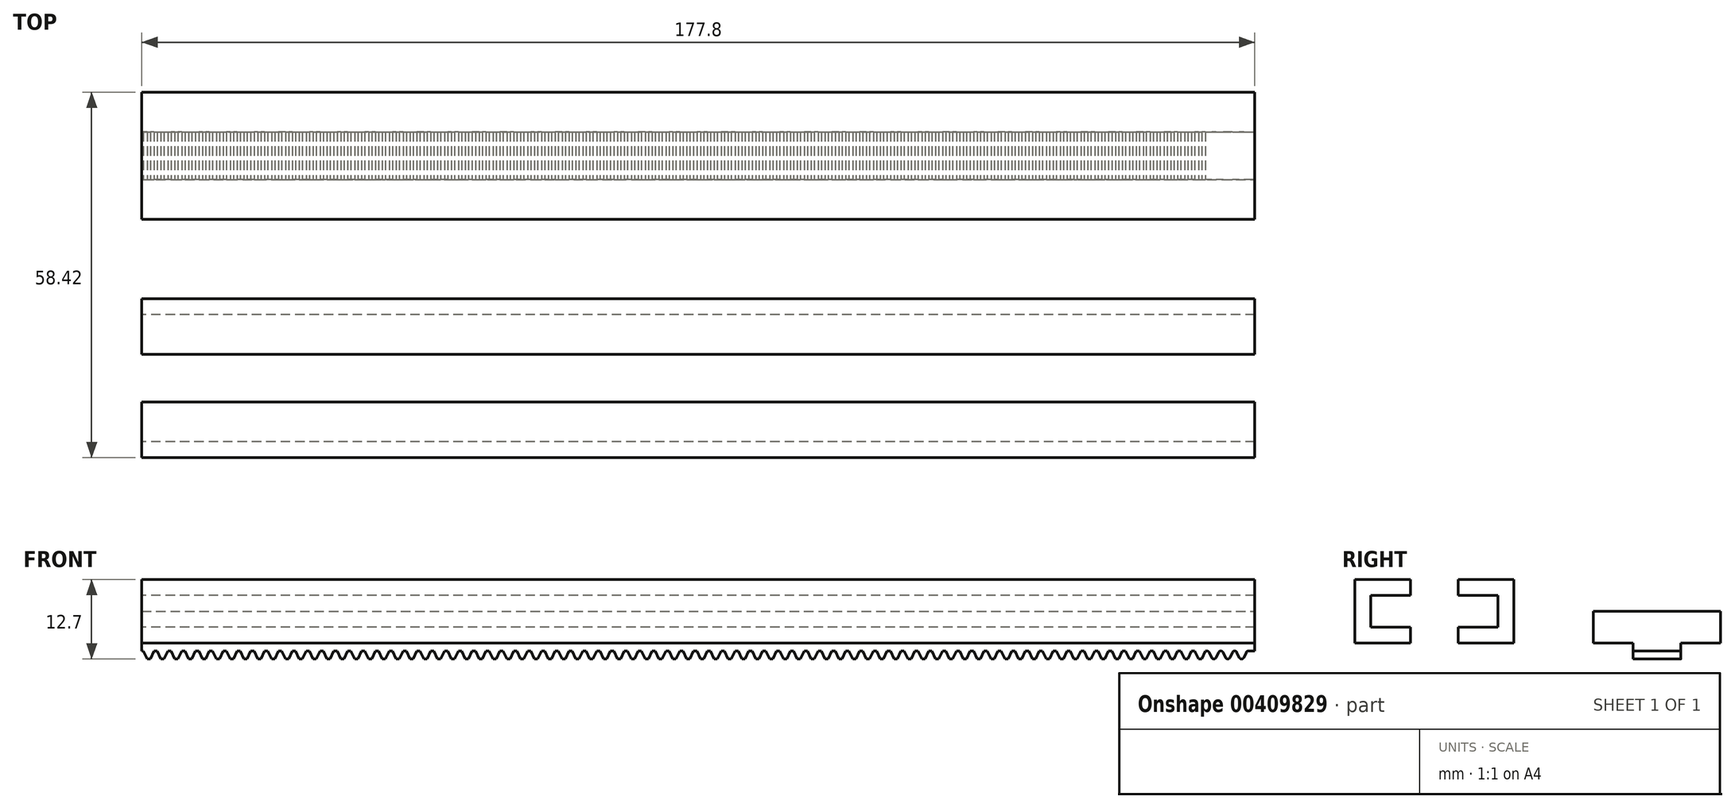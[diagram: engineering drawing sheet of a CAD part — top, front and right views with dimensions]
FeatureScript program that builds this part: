
annotation { "Feature Type Name" : "Feature", "Feature Type Description" : "" }
export const myFeature = defineFeature(function(context is Context, id is Id, definition is map)
    precondition{}
    {
        {
            var Q0;
            Q0=qCreatedBy(makeId("Front.planeOp"),FACE);
            var sketch = newSketch(context, id + "F0", { "sketchPlane" : qUnion([Q0])});
            skLineSegment(sketch, "E0.bottom", {"start": v(0, 0) * mm, "end": v(-177.8, 0) * mm});
            skLineSegment(sketch, "E0.top", {"start": v(0, 10.16) * mm, "end": v(-177.8, 10.16) * mm});
            skLineSegment(sketch, "E0.left", {"start": v(0, 0) * mm, "end": v(0, 10.16) * mm});
            skLineSegment(sketch, "E0.right", {"start": v(-177.8, 0) * mm, "end": v(-177.8, 10.16) * mm});
            skSolve(sketch);
        }
        {
            var Q0;
            Q0=makeQuery(id+"F0.imprint","IMPRINT",FACE,{"disambiguationData":[TD([[makeQuery(id+"F0.imprint","IMPRINT",EDGE,{"derivedFrom":sQuery(id+"F0.wireOp",EDGE,"E0.bottom")}),-1.0]])]});
            extrude(context, id + "F1", {"entities" : qUnion([Q0]), "depth" : 25.4 * mm});
        }
        {
            var Q0;
            Q0=makeQuery(id+"F1.opExtrude","SWEPT_FACE",FACE,{"disambiguationData":[OSD([sQuery(id+"F0.wireOp",EDGE,"E0.right")])]});
            shell(context, id + "F2", {"entities" : qUnion([Q0]), "thickness" : 2.54 * mm});
        }
        {
            var Q0;
            Q0=makeQuery(id+"F2.opShell","OFFSET_FACE",FACE,{"disambiguationData":[OSD([sQuery(id+"F0.wireOp",EDGE,"E0.left")])]});
            extrude(context, id + "F3", {"entities" : qUnion([Q0]), "operationType" : NewBodyOperationType.REMOVE, "oppositeDirection" : true, "depth" : 25.4 * mm});
        }
        {
            var Q0;
            Q0=makeQuery(id+"F1.opExtrude","SWEPT_FACE",FACE,{"disambiguationData":[OSD([sQuery(id+"F0.wireOp",EDGE,"E0.top")])]});
            var sketch = newSketch(context, id + "F4", { "sketchPlane" : qUnion([Q0])});
            skLineSegment(sketch, "E1.bottom", {"start": v(-177.8, -8.9) * mm, "end": v(0, -8.89) * mm});
            skLineSegment(sketch, "E1.top", {"start": v(-177.8, -16.51) * mm, "end": v(0, -16.5) * mm});
            skLineSegment(sketch, "E1.left", {"start": v(-177.8, -8.9) * mm, "end": v(-177.8, -16.51) * mm});
            skLineSegment(sketch, "E1.right", {"start": v(0, -8.89) * mm, "end": v(0, -16.5) * mm});
            skSolve(sketch);
        }
        {
            var Q0;
            Q0=makeQuery(id+"F4.imprint","IMPRINT",FACE,{"disambiguationData":[TD([[makeQuery(id+"F4.imprint","IMPRINT",EDGE,{"derivedFrom":sQuery(id+"F4.wireOp",EDGE,"E1.bottom")}),-1.0]])]});
            extrude(context, id + "F5", {"entities" : qUnion([Q0]), "operationType" : NewBodyOperationType.REMOVE, "oppositeDirection" : true, "depth" : 25.4 * mm});
        }
        {
            var Q0;
            Q0=qCreatedBy(makeId("Right.planeOp"),FACE);
            var sketch = newSketch(context, id + "F6", { "sketchPlane" : qUnion([Q0])});
            skLineSegment(sketch, "E2.bottom", {"start": v(12.7, 0) * mm, "end": v(33.02, 0) * mm});
            skLineSegment(sketch, "E2.top", {"start": v(12.7, 5.08) * mm, "end": v(33.02, 5.08) * mm});
            skLineSegment(sketch, "E2.left", {"start": v(12.7, 0) * mm, "end": v(12.7, 5.08) * mm});
            skLineSegment(sketch, "E2.right", {"start": v(33.02, 0) * mm, "end": v(33.02, 5.08) * mm});
            skLineSegment(sketch, "E3", {"start": v(12.7, 0) * mm, "end": v(19.05, 0) * mm});
            skLineSegment(sketch, "E4", {"start": v(19.05, 0) * mm, "end": v(19.05, -2.54) * mm});
            skLineSegment(sketch, "E5", {"start": v(19.05, -2.54) * mm, "end": v(26.67, -2.54) * mm});
            skLineSegment(sketch, "E6", {"start": v(26.67, -2.54) * mm, "end": v(26.67, 0) * mm});
            skLineSegment(sketch, "E7", {"start": v(26.67, 0) * mm, "end": v(33.02, 0) * mm});
            skSolve(sketch);
        }
        {
            var Q0;
            Q0=makeQuery(id+"F6.imprint","IMPRINT",FACE,{"disambiguationData":[TD([[makeQuery(id+"F6.imprint","IMPRINT",EDGE,{"derivedFrom":sQuery(id+"F6.wireOp",EDGE,"E2.bottom")}),-1.0]])]});
            var Q1;
            Q1=makeQuery(id+"F6.imprint","IMPRINT",FACE,{"disambiguationData":[TD([[makeQuery(id+"F6.imprint","IMPRINT",EDGE,{"derivedFrom":sQuery(id+"F6.wireOp",EDGE,"E2.bottom")}),1.0]])]});
            extrude(context, id + "F7", {"entities" : qUnion([Q0, Q1]), "oppositeDirection" : true, "depth" : 177.8 * mm});
        }
        {
            var Q0;
            Q0=makeQuery(id+"F7.opExtrude","SWEPT_FACE",FACE,{"disambiguationData":[OSD([sQuery(id+"F6.wireOp",EDGE,"E4")])]});
            var sketch = newSketch(context, id + "F8", { "sketchPlane" : qUnion([Q0])});
            skLineSegment(sketch, "E8", {"start": v(-177.8, -1.27) * mm, "end": v(-177.54, -1.27) * mm});
            skLineSegment(sketch, "E9", {"start": v(-177.54, -1.27) * mm, "end": v(-176.94, -2.54) * mm});
            skLineSegment(sketch, "E10", {"start": v(-176.94, -2.54) * mm, "end": v(-176.44, -2.54) * mm});
            skLineSegment(sketch, "E11", {"start": v(-176.44, -2.54) * mm, "end": v(-175.84, -1.27) * mm});
            skLineSegment(sketch, "E12", {"start": v(-175.84, -1.27) * mm, "end": v(-175.6, -1.27) * mm});
            skLineSegment(sketch, "E13.MirrorCS", {"start": v(-175.34, -1.27) * mm, "end": v(-175.6, -1.27) * mm});
            skLineSegment(sketch, "E14.MirrorCS", {"start": v(-174.74, -2.54) * mm, "end": v(-175.34, -1.27) * mm});
            skLineSegment(sketch, "E15.MirrorCS", {"start": v(-174.24, -2.54) * mm, "end": v(-174.74, -2.54) * mm});
            skLineSegment(sketch, "E16.MirrorCS", {"start": v(-173.64, -1.27) * mm, "end": v(-174.24, -2.54) * mm});
            skLineSegment(sketch, "E17.MirrorCS", {"start": v(-173.38, -1.27) * mm, "end": v(-173.64, -1.27) * mm});
            skLineSegment(sketch, "E18.MirrorCS", {"start": v(-173.38, -1.27) * mm, "end": v(-173.12, -1.27) * mm});
            skLineSegment(sketch, "E19.MirrorCS", {"start": v(-173.12, -1.27) * mm, "end": v(-172.52, -2.54) * mm});
            skLineSegment(sketch, "E20.MirrorCS", {"start": v(-172.52, -2.54) * mm, "end": v(-172.02, -2.54) * mm});
            skLineSegment(sketch, "E21.MirrorCS", {"start": v(-172.02, -2.54) * mm, "end": v(-171.42, -1.27) * mm});
            skLineSegment(sketch, "E22.MirrorCS", {"start": v(-171.42, -1.27) * mm, "end": v(-171.17, -1.27) * mm});
            skLineSegment(sketch, "E23.MirrorCS", {"start": v(-170.92, -1.27) * mm, "end": v(-171.17, -1.27) * mm});
            skLineSegment(sketch, "E24.MirrorCS", {"start": v(-170.32, -2.54) * mm, "end": v(-170.92, -1.27) * mm});
            skLineSegment(sketch, "E25.MirrorCS", {"start": v(-169.82, -2.54) * mm, "end": v(-170.32, -2.54) * mm});
            skLineSegment(sketch, "E26.MirrorCS", {"start": v(-169.22, -1.27) * mm, "end": v(-169.82, -2.54) * mm});
            skLineSegment(sketch, "E27.MirrorCS", {"start": v(-168.96, -1.27) * mm, "end": v(-169.22, -1.27) * mm});
            skLineSegment(sketch, "E28.MirrorCS", {"start": v(-164.54, -1.27) * mm, "end": v(-164.28, -1.27) * mm});
            skLineSegment(sketch, "E29.MirrorCS", {"start": v(-164.54, -1.27) * mm, "end": v(-164.8, -1.27) * mm});
            skLineSegment(sketch, "E30.MirrorCS", {"start": v(-162.58, -1.27) * mm, "end": v(-162.33, -1.27) * mm});
            skLineSegment(sketch, "E31.MirrorCS", {"start": v(-162.08, -1.27) * mm, "end": v(-162.33, -1.27) * mm});
            skLineSegment(sketch, "E32.MirrorCS", {"start": v(-160.12, -1.27) * mm, "end": v(-160.38, -1.27) * mm});
            skLineSegment(sketch, "E33.MirrorCS", {"start": v(-161.48, -2.54) * mm, "end": v(-162.08, -1.27) * mm});
            skLineSegment(sketch, "E34.MirrorCS", {"start": v(-160.98, -2.54) * mm, "end": v(-161.48, -2.54) * mm});
            skLineSegment(sketch, "E35.MirrorCS", {"start": v(-160.38, -1.27) * mm, "end": v(-160.98, -2.54) * mm});
            skLineSegment(sketch, "E36.MirrorCS", {"start": v(-166.5, -1.27) * mm, "end": v(-166.75, -1.27) * mm});
            skLineSegment(sketch, "E37.MirrorCS", {"start": v(-168.96, -1.27) * mm, "end": v(-168.7, -1.27) * mm});
            skLineSegment(sketch, "E38.MirrorCS", {"start": v(-167, -1.27) * mm, "end": v(-166.75, -1.27) * mm});
            skLineSegment(sketch, "E39.MirrorCS", {"start": v(-164.8, -1.27) * mm, "end": v(-165.4, -2.54) * mm});
            skLineSegment(sketch, "E40.MirrorCS", {"start": v(-164.28, -1.27) * mm, "end": v(-163.68, -2.54) * mm});
            skLineSegment(sketch, "E41.MirrorCS", {"start": v(-168.7, -1.27) * mm, "end": v(-168.1, -2.54) * mm});
            skLineSegment(sketch, "E42.MirrorCS", {"start": v(-163.68, -2.54) * mm, "end": v(-163.18, -2.54) * mm});
            skLineSegment(sketch, "E43.MirrorCS", {"start": v(-167.6, -2.54) * mm, "end": v(-167, -1.27) * mm});
            skLineSegment(sketch, "E44.MirrorCS", {"start": v(-165.4, -2.54) * mm, "end": v(-165.9, -2.54) * mm});
            skLineSegment(sketch, "E45.MirrorCS", {"start": v(-165.9, -2.54) * mm, "end": v(-166.5, -1.27) * mm});
            skLineSegment(sketch, "E46.MirrorCS", {"start": v(-168.1, -2.54) * mm, "end": v(-167.6, -2.54) * mm});
            skLineSegment(sketch, "E47.MirrorCS", {"start": v(-163.18, -2.54) * mm, "end": v(-162.58, -1.27) * mm});
            skLineSegment(sketch, "E48.MirrorCS", {"start": v(-154.84, -2.54) * mm, "end": v(-154.34, -2.54) * mm});
            skLineSegment(sketch, "E49.MirrorCS", {"start": v(-154.34, -2.54) * mm, "end": v(-153.74, -1.27) * mm});
            skLineSegment(sketch, "E50.MirrorCS", {"start": v(-153.24, -1.27) * mm, "end": v(-153.5, -1.27) * mm});
            skLineSegment(sketch, "E51.MirrorCS", {"start": v(-153.74, -1.27) * mm, "end": v(-153.5, -1.27) * mm});
            skLineSegment(sketch, "E52.MirrorCS", {"start": v(-152.14, -2.54) * mm, "end": v(-152.64, -2.54) * mm});
            skLineSegment(sketch, "E53.MirrorCS", {"start": v(-152.64, -2.54) * mm, "end": v(-153.24, -1.27) * mm});
            skLineSegment(sketch, "E54.MirrorCS", {"start": v(-155.7, -1.27) * mm, "end": v(-155.96, -1.27) * mm});
            skLineSegment(sketch, "E55.MirrorCS", {"start": v(-155.7, -1.27) * mm, "end": v(-155.44, -1.27) * mm});
            skLineSegment(sketch, "E56.MirrorCS", {"start": v(-155.44, -1.27) * mm, "end": v(-154.84, -2.54) * mm});
            skLineSegment(sketch, "E57.MirrorCS", {"start": v(-151.28, -1.27) * mm, "end": v(-151.02, -1.27) * mm});
            skLineSegment(sketch, "E58.MirrorCS", {"start": v(-151.28, -1.27) * mm, "end": v(-151.54, -1.27) * mm});
            skLineSegment(sketch, "E59.MirrorCS", {"start": v(-151.54, -1.27) * mm, "end": v(-152.14, -2.54) * mm});
            skLineSegment(sketch, "E60.MirrorCS", {"start": v(-155.96, -1.27) * mm, "end": v(-156.56, -2.54) * mm});
            skLineSegment(sketch, "E61.MirrorCS", {"start": v(-151.02, -1.27) * mm, "end": v(-150.42, -2.54) * mm});
            skLineSegment(sketch, "E62.MirrorCS", {"start": v(-156.56, -2.54) * mm, "end": v(-157.06, -2.54) * mm});
            skLineSegment(sketch, "E63.MirrorCS", {"start": v(-150.42, -2.54) * mm, "end": v(-149.92, -2.54) * mm});
            skLineSegment(sketch, "E64.MirrorCS", {"start": v(-158.16, -1.27) * mm, "end": v(-157.91, -1.27) * mm});
            skLineSegment(sketch, "E65.MirrorCS", {"start": v(-158.76, -2.54) * mm, "end": v(-158.16, -1.27) * mm});
            skLineSegment(sketch, "E66.MirrorCS", {"start": v(-157.66, -1.27) * mm, "end": v(-157.91, -1.27) * mm});
            skLineSegment(sketch, "E67.MirrorCS", {"start": v(-159.26, -2.54) * mm, "end": v(-158.76, -2.54) * mm});
            skLineSegment(sketch, "E68.MirrorCS", {"start": v(-157.06, -2.54) * mm, "end": v(-157.66, -1.27) * mm});
            skLineSegment(sketch, "E69.MirrorCS", {"start": v(-159.86, -1.27) * mm, "end": v(-159.26, -2.54) * mm});
            skLineSegment(sketch, "E70.MirrorCS", {"start": v(-160.12, -1.27) * mm, "end": v(-159.86, -1.27) * mm});
            skLineSegment(sketch, "E71.MirrorCS", {"start": v(-146.86, -1.27) * mm, "end": v(-146.6, -1.27) * mm});
            skLineSegment(sketch, "E72.MirrorCS", {"start": v(-146.86, -1.27) * mm, "end": v(-147.12, -1.27) * mm});
            skLineSegment(sketch, "E73.MirrorCS", {"start": v(-149.92, -2.54) * mm, "end": v(-149.32, -1.27) * mm});
            skLineSegment(sketch, "E74.MirrorCS", {"start": v(-147.72, -2.54) * mm, "end": v(-148.22, -2.54) * mm});
            skLineSegment(sketch, "E75.MirrorCS", {"start": v(-147.12, -1.27) * mm, "end": v(-147.72, -2.54) * mm});
            skLineSegment(sketch, "E76.MirrorCS", {"start": v(-146.6, -1.27) * mm, "end": v(-146, -2.54) * mm});
            skLineSegment(sketch, "E77.MirrorCS", {"start": v(-145.5, -2.54) * mm, "end": v(-144.9, -1.27) * mm});
            skLineSegment(sketch, "E78.MirrorCS", {"start": v(-144.9, -1.27) * mm, "end": v(-144.65, -1.27) * mm});
            skLineSegment(sketch, "E79.MirrorCS", {"start": v(-144.4, -1.27) * mm, "end": v(-144.65, -1.27) * mm});
            skLineSegment(sketch, "E80.MirrorCS", {"start": v(-143.3, -2.54) * mm, "end": v(-143.8, -2.54) * mm});
            skLineSegment(sketch, "E81.MirrorCS", {"start": v(-142.7, -1.27) * mm, "end": v(-143.3, -2.54) * mm});
            skLineSegment(sketch, "E82.MirrorCS", {"start": v(-148.82, -1.27) * mm, "end": v(-149.07, -1.27) * mm});
            skLineSegment(sketch, "E83.MirrorCS", {"start": v(-148.22, -2.54) * mm, "end": v(-148.82, -1.27) * mm});
            skLineSegment(sketch, "E84.MirrorCS", {"start": v(-149.32, -1.27) * mm, "end": v(-149.07, -1.27) * mm});
            skLineSegment(sketch, "E85.MirrorCS", {"start": v(-146, -2.54) * mm, "end": v(-145.5, -2.54) * mm});
            skLineSegment(sketch, "E86.MirrorCS", {"start": v(-142.44, -1.27) * mm, "end": v(-142.7, -1.27) * mm});
            skLineSegment(sketch, "E87.MirrorCS", {"start": v(-143.8, -2.54) * mm, "end": v(-144.4, -1.27) * mm});
            skLineSegment(sketch, "E88.MirrorCS", {"start": v(-129.18, -1.27) * mm, "end": v(-128.92, -1.27) * mm});
            skLineSegment(sketch, "E89.MirrorCS", {"start": v(-129.18, -1.27) * mm, "end": v(-129.44, -1.27) * mm});
            skLineSegment(sketch, "E90.MirrorCS", {"start": v(-131.14, -1.27) * mm, "end": v(-131.4, -1.27) * mm});
            skLineSegment(sketch, "E91.MirrorCS", {"start": v(-131.64, -1.27) * mm, "end": v(-131.4, -1.27) * mm});
            skLineSegment(sketch, "E92.MirrorCS", {"start": v(-117.88, -1.27) * mm, "end": v(-118.13, -1.27) * mm});
            skLineSegment(sketch, "E93.MirrorCS", {"start": v(-118.38, -1.27) * mm, "end": v(-118.13, -1.27) * mm});
            skLineSegment(sketch, "E94.MirrorCS", {"start": v(-120.34, -1.27) * mm, "end": v(-120.08, -1.27) * mm});
            skLineSegment(sketch, "E95.MirrorCS", {"start": v(-120.34, -1.27) * mm, "end": v(-120.6, -1.27) * mm});
            skLineSegment(sketch, "E96.MirrorCS", {"start": v(-119.48, -2.54) * mm, "end": v(-118.98, -2.54) * mm});
            skLineSegment(sketch, "E97.MirrorCS", {"start": v(-130.54, -2.54) * mm, "end": v(-131.14, -1.27) * mm});
            skLineSegment(sketch, "E98.MirrorCS", {"start": v(-118.98, -2.54) * mm, "end": v(-118.38, -1.27) * mm});
            skLineSegment(sketch, "E99.MirrorCS", {"start": v(-130.04, -2.54) * mm, "end": v(-130.54, -2.54) * mm});
            skLineSegment(sketch, "E100.MirrorCS", {"start": v(-116.78, -2.54) * mm, "end": v(-117.28, -2.54) * mm});
            skLineSegment(sketch, "E101.MirrorCS", {"start": v(-132.74, -2.54) * mm, "end": v(-132.24, -2.54) * mm});
            skLineSegment(sketch, "E102.MirrorCS", {"start": v(-117.28, -2.54) * mm, "end": v(-117.88, -1.27) * mm});
            skLineSegment(sketch, "E103.MirrorCS", {"start": v(-120.08, -1.27) * mm, "end": v(-119.48, -2.54) * mm});
            skLineSegment(sketch, "E104.MirrorCS", {"start": v(-132.24, -2.54) * mm, "end": v(-131.64, -1.27) * mm});
            skLineSegment(sketch, "E105.MirrorCS", {"start": v(-129.44, -1.27) * mm, "end": v(-130.04, -2.54) * mm});
            skLineSegment(sketch, "E106.MirrorCS", {"start": v(-133.34, -1.27) * mm, "end": v(-132.74, -2.54) * mm});
            skLineSegment(sketch, "E107.MirrorCS", {"start": v(-133.6, -1.27) * mm, "end": v(-133.86, -1.27) * mm});
            skLineSegment(sketch, "E108.MirrorCS", {"start": v(-133.6, -1.27) * mm, "end": v(-133.34, -1.27) * mm});
            skLineSegment(sketch, "E109.MirrorCS", {"start": v(-116.18, -1.27) * mm, "end": v(-116.78, -2.54) * mm});
            skLineSegment(sketch, "E110.MirrorCS", {"start": v(-115.92, -1.27) * mm, "end": v(-115.66, -1.27) * mm});
            skLineSegment(sketch, "E111.MirrorCS", {"start": v(-115.92, -1.27) * mm, "end": v(-116.18, -1.27) * mm});
            skLineSegment(sketch, "E112.MirrorCS", {"start": v(-115.66, -1.27) * mm, "end": v(-115.06, -2.54) * mm});
            skLineSegment(sketch, "E113.MirrorCS", {"start": v(-120.6, -1.27) * mm, "end": v(-121.2, -2.54) * mm});
            skLineSegment(sketch, "E114.MirrorCS", {"start": v(-128.92, -1.27) * mm, "end": v(-128.32, -2.54) * mm});
            skLineSegment(sketch, "E115.MirrorCS", {"start": v(-133.86, -1.27) * mm, "end": v(-134.46, -2.54) * mm});
            skLineSegment(sketch, "E116.MirrorCS", {"start": v(-124.76, -1.27) * mm, "end": v(-125.02, -1.27) * mm});
            skLineSegment(sketch, "E117.MirrorCS", {"start": v(-115.06, -2.54) * mm, "end": v(-114.56, -2.54) * mm});
            skLineSegment(sketch, "E118.MirrorCS", {"start": v(-134.46, -2.54) * mm, "end": v(-134.96, -2.54) * mm});
            skLineSegment(sketch, "E119.MirrorCS", {"start": v(-121.2, -2.54) * mm, "end": v(-121.7, -2.54) * mm});
            skLineSegment(sketch, "E120.MirrorCS", {"start": v(-124.76, -1.27) * mm, "end": v(-124.5, -1.27) * mm});
            skLineSegment(sketch, "E121.MirrorCS", {"start": v(-128.32, -2.54) * mm, "end": v(-127.82, -2.54) * mm});
            skLineSegment(sketch, "E122.MirrorCS", {"start": v(-123.9, -2.54) * mm, "end": v(-123.4, -2.54) * mm});
            skLineSegment(sketch, "E123.MirrorCS", {"start": v(-125.62, -2.54) * mm, "end": v(-126.12, -2.54) * mm});
            skLineSegment(sketch, "E124.MirrorCS", {"start": v(-126.12, -2.54) * mm, "end": v(-126.72, -1.27) * mm});
            skLineSegment(sketch, "E125.MirrorCS", {"start": v(-122.3, -1.27) * mm, "end": v(-122.55, -1.27) * mm});
            skLineSegment(sketch, "E126.MirrorCS", {"start": v(-127.22, -1.27) * mm, "end": v(-126.97, -1.27) * mm});
            skLineSegment(sketch, "E127.MirrorCS", {"start": v(-123.4, -2.54) * mm, "end": v(-122.8, -1.27) * mm});
            skLineSegment(sketch, "E128.MirrorCS", {"start": v(-122.8, -1.27) * mm, "end": v(-122.55, -1.27) * mm});
            skLineSegment(sketch, "E129.MirrorCS", {"start": v(-126.72, -1.27) * mm, "end": v(-126.97, -1.27) * mm});
            skLineSegment(sketch, "E130.MirrorCS", {"start": v(-124.5, -1.27) * mm, "end": v(-123.9, -2.54) * mm});
            skLineSegment(sketch, "E131.MirrorCS", {"start": v(-125.02, -1.27) * mm, "end": v(-125.62, -2.54) * mm});
            skLineSegment(sketch, "E132.MirrorCS", {"start": v(-121.7, -2.54) * mm, "end": v(-122.3, -1.27) * mm});
            skLineSegment(sketch, "E133.MirrorCS", {"start": v(-127.82, -2.54) * mm, "end": v(-127.22, -1.27) * mm});
            skLineSegment(sketch, "E134.MirrorCS", {"start": v(-109.04, -1.27) * mm, "end": v(-109.3, -1.27) * mm});
            skLineSegment(sketch, "E135.MirrorCS", {"start": v(-109.54, -1.27) * mm, "end": v(-109.3, -1.27) * mm});
            skLineSegment(sketch, "E136.MirrorCS", {"start": v(-114.56, -2.54) * mm, "end": v(-113.96, -1.27) * mm});
            skLineSegment(sketch, "E137.MirrorCS", {"start": v(-113.46, -1.27) * mm, "end": v(-113.71, -1.27) * mm});
            skLineSegment(sketch, "E138.MirrorCS", {"start": v(-139.98, -1.27) * mm, "end": v(-140.23, -1.27) * mm});
            skLineSegment(sketch, "E139.MirrorCS", {"start": v(-140.48, -1.27) * mm, "end": v(-140.23, -1.27) * mm});
            skLineSegment(sketch, "E140.MirrorCS", {"start": v(-113.96, -1.27) * mm, "end": v(-113.71, -1.27) * mm});
            skLineSegment(sketch, "E141.MirrorCS", {"start": v(-138.02, -1.27) * mm, "end": v(-137.76, -1.27) * mm});
            skLineSegment(sketch, "E142.MirrorCS", {"start": v(-138.02, -1.27) * mm, "end": v(-138.28, -1.27) * mm});
            skLineSegment(sketch, "E143.MirrorCS", {"start": v(-134.96, -2.54) * mm, "end": v(-135.56, -1.27) * mm});
            skLineSegment(sketch, "E144.MirrorCS", {"start": v(-135.56, -1.27) * mm, "end": v(-135.81, -1.27) * mm});
            skLineSegment(sketch, "E145.MirrorCS", {"start": v(-111.5, -1.27) * mm, "end": v(-111.24, -1.27) * mm});
            skLineSegment(sketch, "E146.MirrorCS", {"start": v(-111.5, -1.27) * mm, "end": v(-111.76, -1.27) * mm});
            skLineSegment(sketch, "E147.MirrorCS", {"start": v(-108.44, -2.54) * mm, "end": v(-109.04, -1.27) * mm});
            skLineSegment(sketch, "E148.MirrorCS", {"start": v(-136.06, -1.27) * mm, "end": v(-135.81, -1.27) * mm});
            skLineSegment(sketch, "E149.MirrorCS", {"start": v(-107.08, -1.27) * mm, "end": v(-107.34, -1.27) * mm});
            skLineSegment(sketch, "E150.MirrorCS", {"start": v(-107.94, -2.54) * mm, "end": v(-108.44, -2.54) * mm});
            skLineSegment(sketch, "E151.MirrorCS", {"start": v(-107.34, -1.27) * mm, "end": v(-107.94, -2.54) * mm});
            skLineSegment(sketch, "E152.MirrorCS", {"start": v(-138.28, -1.27) * mm, "end": v(-138.88, -2.54) * mm});
            skLineSegment(sketch, "E153.MirrorCS", {"start": v(-137.76, -1.27) * mm, "end": v(-137.16, -2.54) * mm});
            skLineSegment(sketch, "E154.MirrorCS", {"start": v(-137.16, -2.54) * mm, "end": v(-136.66, -2.54) * mm});
            skLineSegment(sketch, "E155.MirrorCS", {"start": v(-141.08, -2.54) * mm, "end": v(-140.48, -1.27) * mm});
            skLineSegment(sketch, "E156.MirrorCS", {"start": v(-142.44, -1.27) * mm, "end": v(-142.18, -1.27) * mm});
            skLineSegment(sketch, "E157.MirrorCS", {"start": v(-138.88, -2.54) * mm, "end": v(-139.38, -2.54) * mm});
            skLineSegment(sketch, "E158.MirrorCS", {"start": v(-112.86, -2.54) * mm, "end": v(-113.46, -1.27) * mm});
            skLineSegment(sketch, "E159.MirrorCS", {"start": v(-141.58, -2.54) * mm, "end": v(-141.08, -2.54) * mm});
            skLineSegment(sketch, "E160.MirrorCS", {"start": v(-110.14, -2.54) * mm, "end": v(-109.54, -1.27) * mm});
            skLineSegment(sketch, "E161.MirrorCS", {"start": v(-111.24, -1.27) * mm, "end": v(-110.64, -2.54) * mm});
            skLineSegment(sketch, "E162.MirrorCS", {"start": v(-142.18, -1.27) * mm, "end": v(-141.58, -2.54) * mm});
            skLineSegment(sketch, "E163.MirrorCS", {"start": v(-110.64, -2.54) * mm, "end": v(-110.14, -2.54) * mm});
            skLineSegment(sketch, "E164.MirrorCS", {"start": v(-111.76, -1.27) * mm, "end": v(-112.36, -2.54) * mm});
            skLineSegment(sketch, "E165.MirrorCS", {"start": v(-112.36, -2.54) * mm, "end": v(-112.86, -2.54) * mm});
            skLineSegment(sketch, "E166.MirrorCS", {"start": v(-139.38, -2.54) * mm, "end": v(-139.98, -1.27) * mm});
            skLineSegment(sketch, "E167.MirrorCS", {"start": v(-136.66, -2.54) * mm, "end": v(-136.06, -1.27) * mm});
            skLineSegment(sketch, "E168.MirrorCS", {"start": v(-60.42, -1.27) * mm, "end": v(-60.67, -1.27) * mm});
            skLineSegment(sketch, "E169.MirrorCS", {"start": v(-60.93, -1.27) * mm, "end": v(-60.67, -1.27) * mm});
            skLineSegment(sketch, "E170.MirrorCS", {"start": v(-96.28, -1.27) * mm, "end": v(-96.03, -1.27) * mm});
            skLineSegment(sketch, "E171.MirrorCS", {"start": v(-95.78, -1.27) * mm, "end": v(-96.03, -1.27) * mm});
            skLineSegment(sketch, "E172.MirrorCS", {"start": v(-83.02, -1.27) * mm, "end": v(-82.77, -1.27) * mm});
            skLineSegment(sketch, "E173.MirrorCS", {"start": v(-82.52, -1.27) * mm, "end": v(-82.77, -1.27) * mm});
            skLineSegment(sketch, "E174.MirrorCS", {"start": v(-84.98, -1.27) * mm, "end": v(-84.72, -1.27) * mm});
            skLineSegment(sketch, "E175.MirrorCS", {"start": v(-58.46, -1.27) * mm, "end": v(-58.72, -1.27) * mm});
            skLineSegment(sketch, "E176.MirrorCS", {"start": v(-58.46, -1.27) * mm, "end": v(-58.2, -1.27) * mm});
            skLineSegment(sketch, "E177.MirrorCS", {"start": v(-84.98, -1.27) * mm, "end": v(-85.24, -1.27) * mm});
            skLineSegment(sketch, "E178.MirrorCS", {"start": v(-83.62, -2.54) * mm, "end": v(-83.02, -1.27) * mm});
            skLineSegment(sketch, "E179.MirrorCS", {"start": v(-93.82, -1.27) * mm, "end": v(-94.08, -1.27) * mm});
            skLineSegment(sketch, "E180.MirrorCS", {"start": v(-47.16, -1.27) * mm, "end": v(-47.41, -1.27) * mm});
            skLineSegment(sketch, "E181.MirrorCS", {"start": v(-93.82, -1.27) * mm, "end": v(-93.56, -1.27) * mm});
            skLineSegment(sketch, "E182.MirrorCS", {"start": v(-47.67, -1.27) * mm, "end": v(-47.41, -1.27) * mm});
            skLineSegment(sketch, "E183.MirrorCS", {"start": v(-48.77, -2.54) * mm, "end": v(-48.26, -2.54) * mm});
            skLineSegment(sketch, "E184.MirrorCS", {"start": v(-62.88, -1.27) * mm, "end": v(-62.62, -1.27) * mm});
            skLineSegment(sketch, "E185.MirrorCS", {"start": v(-59.82, -2.54) * mm, "end": v(-60.42, -1.27) * mm});
            skLineSegment(sketch, "E186.MirrorCS", {"start": v(-48.26, -2.54) * mm, "end": v(-47.67, -1.27) * mm});
            skLineSegment(sketch, "E187.MirrorCS", {"start": v(-62.88, -1.27) * mm, "end": v(-63.14, -1.27) * mm});
            skLineSegment(sketch, "E188.MirrorCS", {"start": v(-84.13, -2.54) * mm, "end": v(-83.62, -2.54) * mm});
            skLineSegment(sketch, "E189.MirrorCS", {"start": v(-61.52, -2.54) * mm, "end": v(-60.93, -1.27) * mm});
            skLineSegment(sketch, "E190.MirrorCS", {"start": v(-59.32, -2.54) * mm, "end": v(-59.82, -2.54) * mm});
            skLineSegment(sketch, "E191.MirrorCS", {"start": v(-58.72, -1.27) * mm, "end": v(-59.32, -2.54) * mm});
            skLineSegment(sketch, "E192.MirrorCS", {"start": v(-62.62, -1.27) * mm, "end": v(-62.03, -2.54) * mm});
            skLineSegment(sketch, "E193.MirrorCS", {"start": v(-49.62, -1.27) * mm, "end": v(-49.36, -1.27) * mm});
            skLineSegment(sketch, "E194.MirrorCS", {"start": v(-49.62, -1.27) * mm, "end": v(-49.88, -1.27) * mm});
            skLineSegment(sketch, "E195.MirrorCS", {"start": v(-62.03, -2.54) * mm, "end": v(-61.52, -2.54) * mm});
            skLineSegment(sketch, "E196.MirrorCS", {"start": v(-84.72, -1.27) * mm, "end": v(-84.13, -2.54) * mm});
            skLineSegment(sketch, "E197.MirrorCS", {"start": v(-97.38, -2.54) * mm, "end": v(-96.88, -2.54) * mm});
            skLineSegment(sketch, "E198.MirrorCS", {"start": v(-96.88, -2.54) * mm, "end": v(-96.28, -1.27) * mm});
            skLineSegment(sketch, "E199.MirrorCS", {"start": v(-94.68, -2.54) * mm, "end": v(-95.18, -2.54) * mm});
            skLineSegment(sketch, "E200.MirrorCS", {"start": v(-98.24, -1.27) * mm, "end": v(-97.98, -1.27) * mm});
            skLineSegment(sketch, "E201.MirrorCS", {"start": v(-95.18, -2.54) * mm, "end": v(-95.78, -1.27) * mm});
            skLineSegment(sketch, "E202.MirrorCS", {"start": v(-81.42, -2.54) * mm, "end": v(-81.92, -2.54) * mm});
            skLineSegment(sketch, "E203.MirrorCS", {"start": v(-49.36, -1.27) * mm, "end": v(-48.77, -2.54) * mm});
            skLineSegment(sketch, "E204.MirrorCS", {"start": v(-46.06, -2.54) * mm, "end": v(-46.56, -2.54) * mm});
            skLineSegment(sketch, "E205.MirrorCS", {"start": v(-97.98, -1.27) * mm, "end": v(-97.38, -2.54) * mm});
            skLineSegment(sketch, "E206.MirrorCS", {"start": v(-81.92, -2.54) * mm, "end": v(-82.52, -1.27) * mm});
            skLineSegment(sketch, "E207.MirrorCS", {"start": v(-98.24, -1.27) * mm, "end": v(-98.5, -1.27) * mm});
            skLineSegment(sketch, "E208.MirrorCS", {"start": v(-94.08, -1.27) * mm, "end": v(-94.68, -2.54) * mm});
            skLineSegment(sketch, "E209.MirrorCS", {"start": v(-46.56, -2.54) * mm, "end": v(-47.16, -1.27) * mm});
            skLineSegment(sketch, "E210.MirrorCS", {"start": v(-52.09, -1.27) * mm, "end": v(-51.83, -1.27) * mm});
            skLineSegment(sketch, "E211.MirrorCS", {"start": v(-91.36, -1.27) * mm, "end": v(-91.61, -1.27) * mm});
            skLineSegment(sketch, "E212.MirrorCS", {"start": v(-51.58, -1.27) * mm, "end": v(-51.83, -1.27) * mm});
            skLineSegment(sketch, "E213.MirrorCS", {"start": v(-80.82, -1.27) * mm, "end": v(-81.42, -2.54) * mm});
            skLineSegment(sketch, "E214.MirrorCS", {"start": v(-80.56, -1.27) * mm, "end": v(-80.82, -1.27) * mm});
            skLineSegment(sketch, "E215.MirrorCS", {"start": v(-91.86, -1.27) * mm, "end": v(-91.61, -1.27) * mm});
            skLineSegment(sketch, "E216.MirrorCS", {"start": v(-56.5, -1.27) * mm, "end": v(-56.25, -1.27) * mm});
            skLineSegment(sketch, "E217.MirrorCS", {"start": v(-45.2, -1.27) * mm, "end": v(-45.46, -1.27) * mm});
            skLineSegment(sketch, "E218.MirrorCS", {"start": v(-86.94, -1.27) * mm, "end": v(-87.2, -1.27) * mm});
            skLineSegment(sketch, "E219.MirrorCS", {"start": v(-56, -1.27) * mm, "end": v(-56.25, -1.27) * mm});
            skLineSegment(sketch, "E220.MirrorCS", {"start": v(-87.44, -1.27) * mm, "end": v(-87.2, -1.27) * mm});
            skLineSegment(sketch, "E221.MirrorCS", {"start": v(-45.2, -1.27) * mm, "end": v(-44.94, -1.27) * mm});
            skLineSegment(sketch, "E222.MirrorCS", {"start": v(-45.46, -1.27) * mm, "end": v(-46.06, -2.54) * mm});
            skLineSegment(sketch, "E223.MirrorCS", {"start": v(-85.24, -1.27) * mm, "end": v(-85.84, -2.54) * mm});
            skLineSegment(sketch, "E224.MirrorCS", {"start": v(-80.56, -1.27) * mm, "end": v(-80.3, -1.27) * mm});
            skLineSegment(sketch, "E225.MirrorCS", {"start": v(-93.56, -1.27) * mm, "end": v(-92.96, -2.54) * mm});
            skLineSegment(sketch, "E226.MirrorCS", {"start": v(-86.34, -2.54) * mm, "end": v(-86.94, -1.27) * mm});
            skLineSegment(sketch, "E227.MirrorCS", {"start": v(-88.04, -2.54) * mm, "end": v(-87.44, -1.27) * mm});
            skLineSegment(sketch, "E228.MirrorCS", {"start": v(-58.2, -1.27) * mm, "end": v(-57.6, -2.54) * mm});
            skLineSegment(sketch, "E229.MirrorCS", {"start": v(-92.46, -2.54) * mm, "end": v(-91.86, -1.27) * mm});
            skLineSegment(sketch, "E230.MirrorCS", {"start": v(-90.76, -2.54) * mm, "end": v(-91.36, -1.27) * mm});
            skLineSegment(sketch, "E231.MirrorCS", {"start": v(-57.6, -2.54) * mm, "end": v(-57.1, -2.54) * mm});
            skLineSegment(sketch, "E232.MirrorCS", {"start": v(-90.26, -2.54) * mm, "end": v(-90.76, -2.54) * mm});
            skLineSegment(sketch, "E233.MirrorCS", {"start": v(-89.4, -1.27) * mm, "end": v(-89.66, -1.27) * mm});
            skLineSegment(sketch, "E234.MirrorCS", {"start": v(-49.88, -1.27) * mm, "end": v(-50.48, -2.54) * mm});
            skLineSegment(sketch, "E235.MirrorCS", {"start": v(-85.84, -2.54) * mm, "end": v(-86.34, -2.54) * mm});
            skLineSegment(sketch, "E236.MirrorCS", {"start": v(-92.96, -2.54) * mm, "end": v(-92.46, -2.54) * mm});
            skLineSegment(sketch, "E237.MirrorCS", {"start": v(-44.94, -1.27) * mm, "end": v(-44.35, -2.54) * mm});
            skLineSegment(sketch, "E238.MirrorCS", {"start": v(-57.1, -2.54) * mm, "end": v(-56.5, -1.27) * mm});
            skLineSegment(sketch, "E239.MirrorCS", {"start": v(-50.48, -2.54) * mm, "end": v(-50.98, -2.54) * mm});
            skLineSegment(sketch, "E240.MirrorCS", {"start": v(-89.66, -1.27) * mm, "end": v(-90.26, -2.54) * mm});
            skLineSegment(sketch, "E241.MirrorCS", {"start": v(-98.5, -1.27) * mm, "end": v(-99.1, -2.54) * mm});
            skLineSegment(sketch, "E242.MirrorCS", {"start": v(-88.55, -2.54) * mm, "end": v(-88.04, -2.54) * mm});
            skLineSegment(sketch, "E243.MirrorCS", {"start": v(-44.35, -2.54) * mm, "end": v(-43.84, -2.54) * mm});
            skLineSegment(sketch, "E244.MirrorCS", {"start": v(-89.4, -1.27) * mm, "end": v(-89.14, -1.27) * mm});
            skLineSegment(sketch, "E245.MirrorCS", {"start": v(-80.3, -1.27) * mm, "end": v(-79.7, -2.54) * mm});
            skLineSegment(sketch, "E246.MirrorCS", {"start": v(-89.14, -1.27) * mm, "end": v(-88.55, -2.54) * mm});
            skLineSegment(sketch, "E247.MirrorCS", {"start": v(-63.14, -1.27) * mm, "end": v(-63.74, -2.54) * mm});
            skLineSegment(sketch, "E248.MirrorCS", {"start": v(-54.04, -1.27) * mm, "end": v(-54.3, -1.27) * mm});
            skLineSegment(sketch, "E249.MirrorCS", {"start": v(-79.7, -2.54) * mm, "end": v(-79.2, -2.54) * mm});
            skLineSegment(sketch, "E250.MirrorCS", {"start": v(-55.4, -2.54) * mm, "end": v(-56, -1.27) * mm});
            skLineSegment(sketch, "E251.MirrorCS", {"start": v(-99.1, -2.54) * mm, "end": v(-99.6, -2.54) * mm});
            skLineSegment(sketch, "E252.MirrorCS", {"start": v(-54.04, -1.27) * mm, "end": v(-53.78, -1.27) * mm});
            skLineSegment(sketch, "E253.MirrorCS", {"start": v(-63.74, -2.54) * mm, "end": v(-64.24, -2.54) * mm});
            skLineSegment(sketch, "E254.MirrorCS", {"start": v(-53.19, -2.54) * mm, "end": v(-52.68, -2.54) * mm});
            skLineSegment(sketch, "E255.MirrorCS", {"start": v(-50.98, -2.54) * mm, "end": v(-51.58, -1.27) * mm});
            skLineSegment(sketch, "E256.MirrorCS", {"start": v(-54.9, -2.54) * mm, "end": v(-55.4, -2.54) * mm});
            skLineSegment(sketch, "E257.MirrorCS", {"start": v(-52.68, -2.54) * mm, "end": v(-52.09, -1.27) * mm});
            skLineSegment(sketch, "E258.MirrorCS", {"start": v(-54.3, -1.27) * mm, "end": v(-54.9, -2.54) * mm});
            skLineSegment(sketch, "E259.MirrorCS", {"start": v(-53.78, -1.27) * mm, "end": v(-53.19, -2.54) * mm});
            skLineSegment(sketch, "E260.MirrorCS", {"start": v(-42.74, -1.27) * mm, "end": v(-43, -1.27) * mm});
            skLineSegment(sketch, "E261.MirrorCS", {"start": v(-43.25, -1.27) * mm, "end": v(-43, -1.27) * mm});
            skLineSegment(sketch, "E262.MirrorCS", {"start": v(-43.84, -2.54) * mm, "end": v(-43.25, -1.27) * mm});
            skLineSegment(sketch, "E263.MirrorCS", {"start": v(-99.6, -2.54) * mm, "end": v(-100.2, -1.27) * mm});
            skLineSegment(sketch, "E264.MirrorCS", {"start": v(-65.35, -1.27) * mm, "end": v(-65.1, -1.27) * mm});
            skLineSegment(sketch, "E265.MirrorCS", {"start": v(-69.26, -1.27) * mm, "end": v(-69.51, -1.27) * mm});
            skLineSegment(sketch, "E266.MirrorCS", {"start": v(-69.76, -1.27) * mm, "end": v(-69.51, -1.27) * mm});
            skLineSegment(sketch, "E267.MirrorCS", {"start": v(-38.32, -1.27) * mm, "end": v(-38.57, -1.27) * mm});
            skLineSegment(sketch, "E268.MirrorCS", {"start": v(-38.83, -1.27) * mm, "end": v(-38.57, -1.27) * mm});
            skLineSegment(sketch, "E269.MirrorCS", {"start": v(-64.24, -2.54) * mm, "end": v(-64.84, -1.27) * mm});
            skLineSegment(sketch, "E270.MirrorCS", {"start": v(-76.14, -1.27) * mm, "end": v(-76.4, -1.27) * mm});
            skLineSegment(sketch, "E271.MirrorCS", {"start": v(-76.14, -1.27) * mm, "end": v(-75.88, -1.27) * mm});
            skLineSegment(sketch, "E272.MirrorCS", {"start": v(-79.2, -2.54) * mm, "end": v(-78.6, -1.27) * mm});
            skLineSegment(sketch, "E273.MirrorCS", {"start": v(-78.6, -1.27) * mm, "end": v(-78.35, -1.27) * mm});
            skLineSegment(sketch, "E274.MirrorCS", {"start": v(-78.1, -1.27) * mm, "end": v(-78.35, -1.27) * mm});
            skLineSegment(sketch, "E275.MirrorCS", {"start": v(-67.3, -1.27) * mm, "end": v(-67.04, -1.27) * mm});
            skLineSegment(sketch, "E276.MirrorCS", {"start": v(-73.68, -1.27) * mm, "end": v(-73.93, -1.27) * mm});
            skLineSegment(sketch, "E277.MirrorCS", {"start": v(-67.3, -1.27) * mm, "end": v(-67.56, -1.27) * mm});
            skLineSegment(sketch, "E278.MirrorCS", {"start": v(-77, -2.54) * mm, "end": v(-77.5, -2.54) * mm});
            skLineSegment(sketch, "E279.MirrorCS", {"start": v(-74.18, -1.27) * mm, "end": v(-73.93, -1.27) * mm});
            skLineSegment(sketch, "E280.MirrorCS", {"start": v(-71.72, -1.27) * mm, "end": v(-71.46, -1.27) * mm});
            skLineSegment(sketch, "E281.MirrorCS", {"start": v(-76.4, -1.27) * mm, "end": v(-77, -2.54) * mm});
            skLineSegment(sketch, "E282.MirrorCS", {"start": v(-100.7, -1.27) * mm, "end": v(-100.45, -1.27) * mm});
            skLineSegment(sketch, "E283.MirrorCS", {"start": v(-64.84, -1.27) * mm, "end": v(-65.1, -1.27) * mm});
            skLineSegment(sketch, "E284.MirrorCS", {"start": v(-104.62, -1.27) * mm, "end": v(-104.87, -1.27) * mm});
            skLineSegment(sketch, "E285.MirrorCS", {"start": v(-65.94, -2.54) * mm, "end": v(-65.35, -1.27) * mm});
            skLineSegment(sketch, "E286.MirrorCS", {"start": v(-77.5, -2.54) * mm, "end": v(-78.1, -1.27) * mm});
            skLineSegment(sketch, "E287.MirrorCS", {"start": v(-105.12, -1.27) * mm, "end": v(-104.87, -1.27) * mm});
            skLineSegment(sketch, "E288.MirrorCS", {"start": v(-71.72, -1.27) * mm, "end": v(-71.98, -1.27) * mm});
            skLineSegment(sketch, "E289.MirrorCS", {"start": v(-39.42, -2.54) * mm, "end": v(-38.83, -1.27) * mm});
            skLineSegment(sketch, "E290.MirrorCS", {"start": v(-40.78, -1.27) * mm, "end": v(-40.52, -1.27) * mm});
            skLineSegment(sketch, "E291.MirrorCS", {"start": v(-40.78, -1.27) * mm, "end": v(-41.04, -1.27) * mm});
            skLineSegment(sketch, "E292.MirrorCS", {"start": v(-75.29, -2.54) * mm, "end": v(-74.78, -2.54) * mm});
            skLineSegment(sketch, "E293.MirrorCS", {"start": v(-66.45, -2.54) * mm, "end": v(-65.94, -2.54) * mm});
            skLineSegment(sketch, "E294.MirrorCS", {"start": v(-100.2, -1.27) * mm, "end": v(-100.45, -1.27) * mm});
            skLineSegment(sketch, "E295.MirrorCS", {"start": v(-102.66, -1.27) * mm, "end": v(-102.92, -1.27) * mm});
            skLineSegment(sketch, "E296.MirrorCS", {"start": v(-67.04, -1.27) * mm, "end": v(-66.45, -2.54) * mm});
            skLineSegment(sketch, "E297.MirrorCS", {"start": v(-68.66, -2.54) * mm, "end": v(-69.26, -1.27) * mm});
            skLineSegment(sketch, "E298.MirrorCS", {"start": v(-68.16, -2.54) * mm, "end": v(-68.66, -2.54) * mm});
            skLineSegment(sketch, "E299.MirrorCS", {"start": v(-75.88, -1.27) * mm, "end": v(-75.29, -2.54) * mm});
            skLineSegment(sketch, "E300.MirrorCS", {"start": v(-106.82, -1.27) * mm, "end": v(-106.22, -2.54) * mm});
            skLineSegment(sketch, "E301.MirrorCS", {"start": v(-74.78, -2.54) * mm, "end": v(-74.18, -1.27) * mm});
            skLineSegment(sketch, "E302.MirrorCS", {"start": v(-106.22, -2.54) * mm, "end": v(-105.72, -2.54) * mm});
            skLineSegment(sketch, "E303.MirrorCS", {"start": v(-107.08, -1.27) * mm, "end": v(-106.82, -1.27) * mm});
            skLineSegment(sketch, "E304.MirrorCS", {"start": v(-102.66, -1.27) * mm, "end": v(-102.4, -1.27) * mm});
            skLineSegment(sketch, "E305.MirrorCS", {"start": v(-42.15, -2.54) * mm, "end": v(-42.74, -1.27) * mm});
            skLineSegment(sketch, "E306.MirrorCS", {"start": v(-36.36, -1.27) * mm, "end": v(-36.62, -1.27) * mm});
            skLineSegment(sketch, "E307.MirrorCS", {"start": v(-36.62, -1.27) * mm, "end": v(-37.22, -2.54) * mm});
            skLineSegment(sketch, "E308.MirrorCS", {"start": v(-37.22, -2.54) * mm, "end": v(-37.73, -2.54) * mm});
            skLineSegment(sketch, "E309.MirrorCS", {"start": v(-37.73, -2.54) * mm, "end": v(-38.32, -1.27) * mm});
            skLineSegment(sketch, "E310.MirrorCS", {"start": v(-39.93, -2.54) * mm, "end": v(-39.42, -2.54) * mm});
            skLineSegment(sketch, "E311.MirrorCS", {"start": v(-40.52, -1.27) * mm, "end": v(-39.93, -2.54) * mm});
            skLineSegment(sketch, "E312.MirrorCS", {"start": v(-41.04, -1.27) * mm, "end": v(-41.64, -2.54) * mm});
            skLineSegment(sketch, "E313.MirrorCS", {"start": v(-105.72, -2.54) * mm, "end": v(-105.12, -1.27) * mm});
            skLineSegment(sketch, "E314.MirrorCS", {"start": v(-103.52, -2.54) * mm, "end": v(-104.02, -2.54) * mm});
            skLineSegment(sketch, "E315.MirrorCS", {"start": v(-104.02, -2.54) * mm, "end": v(-104.62, -1.27) * mm});
            skLineSegment(sketch, "E316.MirrorCS", {"start": v(-67.56, -1.27) * mm, "end": v(-68.16, -2.54) * mm});
            skLineSegment(sketch, "E317.MirrorCS", {"start": v(-70.87, -2.54) * mm, "end": v(-70.36, -2.54) * mm});
            skLineSegment(sketch, "E318.MirrorCS", {"start": v(-72.58, -2.54) * mm, "end": v(-73.08, -2.54) * mm});
            skLineSegment(sketch, "E319.MirrorCS", {"start": v(-102.92, -1.27) * mm, "end": v(-103.52, -2.54) * mm});
            skLineSegment(sketch, "E320.MirrorCS", {"start": v(-73.08, -2.54) * mm, "end": v(-73.68, -1.27) * mm});
            skLineSegment(sketch, "E321.MirrorCS", {"start": v(-70.36, -2.54) * mm, "end": v(-69.76, -1.27) * mm});
            skLineSegment(sketch, "E322.MirrorCS", {"start": v(-101.8, -2.54) * mm, "end": v(-101.3, -2.54) * mm});
            skLineSegment(sketch, "E323.MirrorCS", {"start": v(-71.46, -1.27) * mm, "end": v(-70.87, -2.54) * mm});
            skLineSegment(sketch, "E324.MirrorCS", {"start": v(-71.98, -1.27) * mm, "end": v(-72.58, -2.54) * mm});
            skLineSegment(sketch, "E325.MirrorCS", {"start": v(-41.64, -2.54) * mm, "end": v(-42.15, -2.54) * mm});
            skLineSegment(sketch, "E326.MirrorCS", {"start": v(-101.3, -2.54) * mm, "end": v(-100.7, -1.27) * mm});
            skLineSegment(sketch, "E327.MirrorCS", {"start": v(-102.4, -1.27) * mm, "end": v(-101.8, -2.54) * mm});
            skLineSegment(sketch, "E328", {"start": v(-36.36, -1.27) * mm, "end": v(-36.36, -2.54) * mm});
            skLineSegment(sketch, "E329.MirrorCS", {"start": v(-11.8, -1.27) * mm, "end": v(-12.05, -1.27) * mm});
            skLineSegment(sketch, "E330.MirrorCS", {"start": v(-25.06, -1.27) * mm, "end": v(-25.31, -1.27) * mm});
            skLineSegment(sketch, "E331.MirrorCS", {"start": v(-12.3, -1.27) * mm, "end": v(-12.05, -1.27) * mm});
            skLineSegment(sketch, "E332.MirrorCS", {"start": v(-25.57, -1.27) * mm, "end": v(-25.31, -1.27) * mm});
            skLineSegment(sketch, "E333.MirrorCS", {"start": v(-14.26, -1.27) * mm, "end": v(-14, -1.27) * mm});
            skLineSegment(sketch, "E334.MirrorCS", {"start": v(-23.96, -2.54) * mm, "end": v(-24.47, -2.54) * mm});
            skLineSegment(sketch, "E335.MirrorCS", {"start": v(-13.4, -2.54) * mm, "end": v(-12.9, -2.54) * mm});
            skLineSegment(sketch, "E336.MirrorCS", {"start": v(-14.26, -1.27) * mm, "end": v(-14.53, -1.27) * mm});
            skLineSegment(sketch, "E337.MirrorCS", {"start": v(-26.67, -2.54) * mm, "end": v(-26.16, -2.54) * mm});
            skLineSegment(sketch, "E338.MirrorCS", {"start": v(-23.1, -1.27) * mm, "end": v(-22.84, -1.27) * mm});
            skLineSegment(sketch, "E339.MirrorCS", {"start": v(-23.1, -1.27) * mm, "end": v(-23.36, -1.27) * mm});
            skLineSegment(sketch, "E340.MirrorCS", {"start": v(-27.52, -1.27) * mm, "end": v(-27.78, -1.27) * mm});
            skLineSegment(sketch, "E341.MirrorCS", {"start": v(-27.52, -1.27) * mm, "end": v(-27.26, -1.27) * mm});
            skLineSegment(sketch, "E342.MirrorCS", {"start": v(-20.64, -1.27) * mm, "end": v(-20.9, -1.27) * mm});
            skLineSegment(sketch, "E343.MirrorCS", {"start": v(-21.15, -1.27) * mm, "end": v(-20.9, -1.27) * mm});
            skLineSegment(sketch, "E344.MirrorCS", {"start": v(-16.73, -1.27) * mm, "end": v(-16.47, -1.27) * mm});
            skLineSegment(sketch, "E345.MirrorCS", {"start": v(-16.22, -1.27) * mm, "end": v(-16.47, -1.27) * mm});
            skLineSegment(sketch, "E346.MirrorCS", {"start": v(-19.54, -2.54) * mm, "end": v(-20.05, -2.54) * mm});
            skLineSegment(sketch, "E347.MirrorCS", {"start": v(-17.83, -2.54) * mm, "end": v(-17.32, -2.54) * mm});
            skLineSegment(sketch, "E348.MirrorCS", {"start": v(-22.25, -2.54) * mm, "end": v(-21.74, -2.54) * mm});
            skLineSegment(sketch, "E349.MirrorCS", {"start": v(-15.12, -2.54) * mm, "end": v(-15.63, -2.54) * mm});
            skLineSegment(sketch, "E350.MirrorCS", {"start": v(-18.68, -1.27) * mm, "end": v(-18.95, -1.27) * mm});
            skLineSegment(sketch, "E351.MirrorCS", {"start": v(-28.38, -2.54) * mm, "end": v(-28.89, -2.54) * mm});
            skLineSegment(sketch, "E352.MirrorCS", {"start": v(-18.68, -1.27) * mm, "end": v(-18.42, -1.27) * mm});
            skLineSegment(sketch, "E353.MirrorCS", {"start": v(-24.47, -2.54) * mm, "end": v(-25.06, -1.27) * mm});
            skLineSegment(sketch, "E354.MirrorCS", {"start": v(-12.9, -2.54) * mm, "end": v(-12.3, -1.27) * mm});
            skLineSegment(sketch, "E355.MirrorCS", {"start": v(-26.16, -2.54) * mm, "end": v(-25.57, -1.27) * mm});
            skLineSegment(sketch, "E356.MirrorCS", {"start": v(-11.2, -2.54) * mm, "end": v(-11.8, -1.27) * mm});
            skLineSegment(sketch, "E357.MirrorCS", {"start": v(-27.26, -1.27) * mm, "end": v(-26.67, -2.54) * mm});
            skLineSegment(sketch, "E358.MirrorCS", {"start": v(-22.84, -1.27) * mm, "end": v(-22.25, -2.54) * mm});
            skLineSegment(sketch, "E359.MirrorCS", {"start": v(-14, -1.27) * mm, "end": v(-13.4, -2.54) * mm});
            skLineSegment(sketch, "E360.MirrorCS", {"start": v(-23.36, -1.27) * mm, "end": v(-23.96, -2.54) * mm});
            skLineSegment(sketch, "E361.MirrorCS", {"start": v(-14.53, -1.27) * mm, "end": v(-15.12, -2.54) * mm});
            skLineSegment(sketch, "E362.MirrorCS", {"start": v(-27.78, -1.27) * mm, "end": v(-28.38, -2.54) * mm});
            skLineSegment(sketch, "E363.MirrorCS", {"start": v(-29.99, -1.27) * mm, "end": v(-29.73, -1.27) * mm});
            skLineSegment(sketch, "E364.MirrorCS", {"start": v(-35.5, -2.54) * mm, "end": v(-35, -2.54) * mm});
            skLineSegment(sketch, "E365.MirrorCS", {"start": v(-31.94, -1.27) * mm, "end": v(-31.68, -1.27) * mm});
            skLineSegment(sketch, "E366.MirrorCS", {"start": v(-31.94, -1.27) * mm, "end": v(-32.2, -1.27) * mm});
            skLineSegment(sketch, "E367.MirrorCS", {"start": v(-36.36, -1.27) * mm, "end": v(-36.1, -1.27) * mm});
            skLineSegment(sketch, "E368.MirrorCS", {"start": v(-20.05, -2.54) * mm, "end": v(-20.64, -1.27) * mm});
            skLineSegment(sketch, "E369.MirrorCS", {"start": v(-33.9, -1.27) * mm, "end": v(-34.15, -1.27) * mm});
            skLineSegment(sketch, "E370.MirrorCS", {"start": v(-34.4, -1.27) * mm, "end": v(-34.15, -1.27) * mm});
            skLineSegment(sketch, "E371.MirrorCS", {"start": v(-31.09, -2.54) * mm, "end": v(-30.58, -2.54) * mm});
            skLineSegment(sketch, "E372.MirrorCS", {"start": v(-32.8, -2.54) * mm, "end": v(-33.3, -2.54) * mm});
            skLineSegment(sketch, "E373.MirrorCS", {"start": v(-29.48, -1.27) * mm, "end": v(-29.73, -1.27) * mm});
            skLineSegment(sketch, "E374.MirrorCS", {"start": v(-17.32, -2.54) * mm, "end": v(-16.73, -1.27) * mm});
            skLineSegment(sketch, "E375.MirrorCS", {"start": v(-18.42, -1.27) * mm, "end": v(-17.83, -2.54) * mm});
            skLineSegment(sketch, "E376.MirrorCS", {"start": v(-15.63, -2.54) * mm, "end": v(-16.22, -1.27) * mm});
            skLineSegment(sketch, "E377.MirrorCS", {"start": v(-18.95, -1.27) * mm, "end": v(-19.54, -2.54) * mm});
            skLineSegment(sketch, "E378.MirrorCS", {"start": v(-21.74, -2.54) * mm, "end": v(-21.15, -1.27) * mm});
            skLineSegment(sketch, "E379.MirrorCS", {"start": v(-36.1, -1.27) * mm, "end": v(-35.5, -2.54) * mm});
            skLineSegment(sketch, "E380.MirrorCS", {"start": v(-33.3, -2.54) * mm, "end": v(-33.9, -1.27) * mm});
            skLineSegment(sketch, "E381.MirrorCS", {"start": v(-30.58, -2.54) * mm, "end": v(-29.99, -1.27) * mm});
            skLineSegment(sketch, "E382.MirrorCS", {"start": v(-35, -2.54) * mm, "end": v(-34.4, -1.27) * mm});
            skLineSegment(sketch, "E383.MirrorCS", {"start": v(-32.2, -1.27) * mm, "end": v(-32.8, -2.54) * mm});
            skLineSegment(sketch, "E384.MirrorCS", {"start": v(-31.68, -1.27) * mm, "end": v(-31.09, -2.54) * mm});
            skLineSegment(sketch, "E385.MirrorCS", {"start": v(-28.89, -2.54) * mm, "end": v(-29.48, -1.27) * mm});
            skLineSegment(sketch, "E386.MirrorCS", {"start": v(-10.7, -2.54) * mm, "end": v(-11.2, -2.54) * mm});
            skLineSegment(sketch, "E387.MirrorCS", {"start": v(-10.1, -1.27) * mm, "end": v(-10.7, -2.54) * mm});
            skLineSegment(sketch, "E388.MirrorCS", {"start": v(-9.84, -1.27) * mm, "end": v(-10.1, -1.27) * mm});
            skLineSegment(sketch, "E389.MirrorCS", {"start": v(-9.84, -1.27) * mm, "end": v(-9.58, -1.27) * mm});
            skLineSegment(sketch, "E390.MirrorCS", {"start": v(-8.99, -2.54) * mm, "end": v(-8.48, -2.54) * mm});
            skLineSegment(sketch, "E391.MirrorCS", {"start": v(-7.89, -1.27) * mm, "end": v(-7.63, -1.27) * mm});
            skLineSegment(sketch, "E392.MirrorCS", {"start": v(-7.38, -1.27) * mm, "end": v(-7.63, -1.27) * mm});
            skLineSegment(sketch, "E393.MirrorCS", {"start": v(-2.96, -1.27) * mm, "end": v(-3.21, -1.27) * mm});
            skLineSegment(sketch, "E394.MirrorCS", {"start": v(-3.47, -1.27) * mm, "end": v(-3.21, -1.27) * mm});
            skLineSegment(sketch, "E395.MirrorCS", {"start": v(-9.58, -1.27) * mm, "end": v(-8.99, -2.54) * mm});
            skLineSegment(sketch, "E396.MirrorCS", {"start": v(-5.42, -1.27) * mm, "end": v(-5.69, -1.27) * mm});
            skLineSegment(sketch, "E397.MirrorCS", {"start": v(-1.86, -2.54) * mm, "end": v(-2.37, -2.54) * mm});
            skLineSegment(sketch, "E398.MirrorCS", {"start": v(-4.57, -2.54) * mm, "end": v(-4.06, -2.54) * mm});
            skLineSegment(sketch, "E399.MirrorCS", {"start": v(-6.28, -2.54) * mm, "end": v(-6.79, -2.54) * mm});
            skLineSegment(sketch, "E400.MirrorCS", {"start": v(-5.42, -1.27) * mm, "end": v(-5.16, -1.27) * mm});
            skLineSegment(sketch, "E401.MirrorCS", {"start": v(-2.37, -2.54) * mm, "end": v(-2.96, -1.27) * mm});
            skLineSegment(sketch, "E402.MirrorCS", {"start": v(-8.48, -2.54) * mm, "end": v(-7.89, -1.27) * mm});
            skLineSegment(sketch, "E403.MirrorCS", {"start": v(-6.79, -2.54) * mm, "end": v(-7.38, -1.27) * mm});
            skLineSegment(sketch, "E404.MirrorCS", {"start": v(-5.16, -1.27) * mm, "end": v(-4.57, -2.54) * mm});
            skLineSegment(sketch, "E405.MirrorCS", {"start": v(-4.06, -2.54) * mm, "end": v(-3.47, -1.27) * mm});
            skLineSegment(sketch, "E406.MirrorCS", {"start": v(-5.69, -1.27) * mm, "end": v(-6.28, -2.54) * mm});
            skLineSegment(sketch, "E407.MirrorCS", {"start": v(-1, -1.27) * mm, "end": v(-0.74, -1.27) * mm});
            skLineSegment(sketch, "E408.MirrorCS", {"start": v(-1, -1.27) * mm, "end": v(-1.27, -1.27) * mm});
            skLineSegment(sketch, "E409.MirrorCS", {"start": v(-1.27, -1.27) * mm, "end": v(-1.86, -2.54) * mm});
            skLineSegment(sketch, "E410", {"start": v(-0.74, -1.27) * mm, "end": v(0, -1.27) * mm});
            skSolve(sketch);
        }
        {
            var Q0;
            Q0=makeQuery(id+"F8.imprint","IMPRINT",FACE,{"disambiguationData":[TD([[makeQuery(id+"F8.imprint","IMPRINT",EDGE,{"derivedFrom":sQuery(id+"F8.wireOp",EDGE,"E407.MirrorCS")}),-1.0]])]});
            var Q1;
            Q1=makeQuery(id+"F8.imprint","IMPRINT",FACE,{"disambiguationData":[TD([[makeQuery(id+"F8.imprint","IMPRINT",EDGE,{"derivedFrom":sQuery(id+"F8.wireOp",EDGE,"E394.MirrorCS")}),-1.0]])]});
            var Q2;
            Q2=makeQuery(id+"F8.imprint","IMPRINT",FACE,{"disambiguationData":[TD([[makeQuery(id+"F8.imprint","IMPRINT",EDGE,{"derivedFrom":sQuery(id+"F8.wireOp",EDGE,"E396.MirrorCS")}),1.0]])]});
            var Q3;
            {var subQ1=sQuery(id+"F8.wireOp",EDGE,"E402.MirrorCS");Q3=makeQuery(id+"F8.imprint","IMPRINT",FACE,{"disambiguationData":[TD([[makeQuery(id+"F8.imprint","IMPRINT",EDGE,{"derivedFrom":subQ1}),-1.0]])]});}
            var Q4;
            Q4=makeQuery(id+"F8.imprint","IMPRINT",FACE,{"disambiguationData":[TD([[makeQuery(id+"F8.imprint","IMPRINT",EDGE,{"derivedFrom":sQuery(id+"F8.wireOp",EDGE,"E388.MirrorCS")}),1.0]])]});
            var Q5;
            Q5=makeQuery(id+"F8.imprint","IMPRINT",FACE,{"disambiguationData":[TD([[makeQuery(id+"F8.imprint","IMPRINT",EDGE,{"derivedFrom":sQuery(id+"F8.wireOp",EDGE,"E331.MirrorCS")}),-1.0]])]});
            var Q6;
            Q6=makeQuery(id+"F8.imprint","IMPRINT",FACE,{"disambiguationData":[TD([[makeQuery(id+"F8.imprint","IMPRINT",EDGE,{"derivedFrom":sQuery(id+"F8.wireOp",EDGE,"E336.MirrorCS")}),1.0]])]});
            var Q7;
            Q7=makeQuery(id+"F8.imprint","IMPRINT",FACE,{"disambiguationData":[TD([[makeQuery(id+"F8.imprint","IMPRINT",EDGE,{"derivedFrom":sQuery(id+"F8.wireOp",EDGE,"E345.MirrorCS")}),1.0]])]});
            var Q8;
            Q8=makeQuery(id+"F8.imprint","IMPRINT",FACE,{"disambiguationData":[TD([[makeQuery(id+"F8.imprint","IMPRINT",EDGE,{"derivedFrom":sQuery(id+"F8.wireOp",EDGE,"E352.MirrorCS")}),-1.0]])]});
            var Q9;
            Q9=makeQuery(id+"F8.imprint","IMPRINT",FACE,{"disambiguationData":[TD([[makeQuery(id+"F8.imprint","IMPRINT",EDGE,{"derivedFrom":sQuery(id+"F8.wireOp",EDGE,"E342.MirrorCS")}),1.0]])]});
            var Q10;
            Q10=makeQuery(id+"F8.imprint","IMPRINT",FACE,{"disambiguationData":[TD([[makeQuery(id+"F8.imprint","IMPRINT",EDGE,{"derivedFrom":sQuery(id+"F8.wireOp",EDGE,"E339.MirrorCS")}),1.0]])]});
            var Q11;
            Q11=makeQuery(id+"F8.imprint","IMPRINT",FACE,{"disambiguationData":[TD([[makeQuery(id+"F8.imprint","IMPRINT",EDGE,{"derivedFrom":sQuery(id+"F8.wireOp",EDGE,"E330.MirrorCS")}),1.0]])]});
            var Q12;
            Q12=makeQuery(id+"F8.imprint","IMPRINT",FACE,{"disambiguationData":[TD([[makeQuery(id+"F8.imprint","IMPRINT",EDGE,{"derivedFrom":sQuery(id+"F8.wireOp",EDGE,"E340.MirrorCS")}),1.0]])]});
            var Q13;
            Q13=makeQuery(id+"F8.imprint","IMPRINT",FACE,{"disambiguationData":[TD([[makeQuery(id+"F8.imprint","IMPRINT",EDGE,{"derivedFrom":sQuery(id+"F8.wireOp",EDGE,"E363.MirrorCS")}),-1.0]])]});
            var Q14;
            Q14=makeQuery(id+"F8.imprint","IMPRINT",FACE,{"disambiguationData":[TD([[makeQuery(id+"F8.imprint","IMPRINT",EDGE,{"derivedFrom":sQuery(id+"F8.wireOp",EDGE,"E365.MirrorCS")}),-1.0]])]});
            var Q15;
            Q15=makeQuery(id+"F8.imprint","IMPRINT",FACE,{"disambiguationData":[TD([[makeQuery(id+"F8.imprint","IMPRINT",EDGE,{"derivedFrom":sQuery(id+"F8.wireOp",EDGE,"E369.MirrorCS")}),1.0]])]});
            var Q16;
            {var subQ0=sQuery(id+"F8.wireOp",EDGE,"E328");Q16=makeQuery(id+"F8.imprint","IMPRINT",FACE,{"disambiguationData":[TD([[makeQuery(id+"F8.imprint","IMPRINT",EDGE,{"derivedFrom":subQ0}),1.0]])]});}
            var Q17;
            Q17=makeQuery(id+"F8.imprint","IMPRINT",FACE,{"disambiguationData":[TD([[makeQuery(id+"F8.imprint","IMPRINT",EDGE,{"derivedFrom":sQuery(id+"F8.wireOp",EDGE,"E306.MirrorCS")}),1.0]])]});
            var Q18;
            Q18=makeQuery(id+"F8.imprint","IMPRINT",FACE,{"disambiguationData":[TD([[makeQuery(id+"F8.imprint","IMPRINT",EDGE,{"derivedFrom":sQuery(id+"F8.wireOp",EDGE,"E267.MirrorCS")}),1.0]])]});
            var Q19;
            Q19=makeQuery(id+"F8.imprint","IMPRINT",FACE,{"disambiguationData":[TD([[makeQuery(id+"F8.imprint","IMPRINT",EDGE,{"derivedFrom":sQuery(id+"F8.wireOp",EDGE,"E290.MirrorCS")}),-1.0]])]});
            var Q20;
            Q20=makeQuery(id+"F8.imprint","IMPRINT",FACE,{"disambiguationData":[TD([[makeQuery(id+"F8.imprint","IMPRINT",EDGE,{"derivedFrom":sQuery(id+"F8.wireOp",EDGE,"E260.MirrorCS")}),1.0]])]});
            var Q21;
            Q21=makeQuery(id+"F8.imprint","IMPRINT",FACE,{"disambiguationData":[TD([[makeQuery(id+"F8.imprint","IMPRINT",EDGE,{"derivedFrom":sQuery(id+"F8.wireOp",EDGE,"E221.MirrorCS")}),-1.0]])]});
            var Q22;
            Q22=makeQuery(id+"F8.imprint","IMPRINT",FACE,{"disambiguationData":[TD([[makeQuery(id+"F8.imprint","IMPRINT",EDGE,{"derivedFrom":sQuery(id+"F8.wireOp",EDGE,"E182.MirrorCS")}),-1.0]])]});
            var Q23;
            Q23=makeQuery(id+"F8.imprint","IMPRINT",FACE,{"disambiguationData":[TD([[makeQuery(id+"F8.imprint","IMPRINT",EDGE,{"derivedFrom":sQuery(id+"F8.wireOp",EDGE,"E193.MirrorCS")}),-1.0]])]});
            var Q24;
            Q24=makeQuery(id+"F8.imprint","IMPRINT",FACE,{"disambiguationData":[TD([[makeQuery(id+"F8.imprint","IMPRINT",EDGE,{"derivedFrom":sQuery(id+"F8.wireOp",EDGE,"E212.MirrorCS")}),1.0]])]});
            var Q25;
            Q25=makeQuery(id+"F8.imprint","IMPRINT",FACE,{"disambiguationData":[TD([[makeQuery(id+"F8.imprint","IMPRINT",EDGE,{"derivedFrom":sQuery(id+"F8.wireOp",EDGE,"E248.MirrorCS")}),1.0]])]});
            var Q26;
            Q26=makeQuery(id+"F8.imprint","IMPRINT",FACE,{"disambiguationData":[TD([[makeQuery(id+"F8.imprint","IMPRINT",EDGE,{"derivedFrom":sQuery(id+"F8.wireOp",EDGE,"E219.MirrorCS")}),1.0]])]});
            var Q27;
            Q27=makeQuery(id+"F8.imprint","IMPRINT",FACE,{"disambiguationData":[TD([[makeQuery(id+"F8.imprint","IMPRINT",EDGE,{"derivedFrom":sQuery(id+"F8.wireOp",EDGE,"E175.MirrorCS")}),1.0]])]});
            var Q28;
            Q28=makeQuery(id+"F8.imprint","IMPRINT",FACE,{"disambiguationData":[TD([[makeQuery(id+"F8.imprint","IMPRINT",EDGE,{"derivedFrom":sQuery(id+"F8.wireOp",EDGE,"E168.MirrorCS")}),1.0]])]});
            var Q29;
            Q29=makeQuery(id+"F8.imprint","IMPRINT",FACE,{"disambiguationData":[TD([[makeQuery(id+"F8.imprint","IMPRINT",EDGE,{"derivedFrom":sQuery(id+"F8.wireOp",EDGE,"E187.MirrorCS")}),1.0]])]});
            var Q30;
            Q30=makeQuery(id+"F8.imprint","IMPRINT",FACE,{"disambiguationData":[TD([[makeQuery(id+"F8.imprint","IMPRINT",EDGE,{"derivedFrom":sQuery(id+"F8.wireOp",EDGE,"E264.MirrorCS")}),-1.0]])]});
            var Q31;
            Q31=makeQuery(id+"F8.imprint","IMPRINT",FACE,{"disambiguationData":[TD([[makeQuery(id+"F8.imprint","IMPRINT",EDGE,{"derivedFrom":sQuery(id+"F8.wireOp",EDGE,"E275.MirrorCS")}),-1.0]])]});
            var Q32;
            Q32=makeQuery(id+"F8.imprint","IMPRINT",FACE,{"disambiguationData":[TD([[makeQuery(id+"F8.imprint","IMPRINT",EDGE,{"derivedFrom":sQuery(id+"F8.wireOp",EDGE,"E265.MirrorCS")}),1.0]])]});
            var Q33;
            Q33=makeQuery(id+"F8.imprint","IMPRINT",FACE,{"disambiguationData":[TD([[makeQuery(id+"F8.imprint","IMPRINT",EDGE,{"derivedFrom":sQuery(id+"F8.wireOp",EDGE,"E280.MirrorCS")}),-1.0]])]});
            var Q34;
            Q34=makeQuery(id+"F8.imprint","IMPRINT",FACE,{"disambiguationData":[TD([[makeQuery(id+"F8.imprint","IMPRINT",EDGE,{"derivedFrom":sQuery(id+"F8.wireOp",EDGE,"E276.MirrorCS")}),1.0]])]});
            var Q35;
            Q35=makeQuery(id+"F8.imprint","IMPRINT",FACE,{"disambiguationData":[TD([[makeQuery(id+"F8.imprint","IMPRINT",EDGE,{"derivedFrom":sQuery(id+"F8.wireOp",EDGE,"E270.MirrorCS")}),1.0]])]});
            var Q36;
            {var subQ1=sQuery(id+"F8.wireOp",EDGE,"E272.MirrorCS");Q36=makeQuery(id+"F8.imprint","IMPRINT",FACE,{"disambiguationData":[TD([[makeQuery(id+"F8.imprint","IMPRINT",EDGE,{"derivedFrom":subQ1}),-1.0]])]});}
            var Q37;
            {var subQ1=sQuery(id+"F8.wireOp",EDGE,"E213.MirrorCS");Q37=makeQuery(id+"F8.imprint","IMPRINT",FACE,{"disambiguationData":[TD([[makeQuery(id+"F8.imprint","IMPRINT",EDGE,{"derivedFrom":subQ1}),1.0]])]});}
            var Q38;
            Q38=makeQuery(id+"F8.imprint","IMPRINT",FACE,{"disambiguationData":[TD([[makeQuery(id+"F8.imprint","IMPRINT",EDGE,{"derivedFrom":sQuery(id+"F8.wireOp",EDGE,"E173.MirrorCS")}),1.0]])]});
            var Q39;
            Q39=makeQuery(id+"F8.imprint","IMPRINT",FACE,{"disambiguationData":[TD([[makeQuery(id+"F8.imprint","IMPRINT",EDGE,{"derivedFrom":sQuery(id+"F8.wireOp",EDGE,"E177.MirrorCS")}),1.0]])]});
            var Q40;
            Q40=makeQuery(id+"F8.imprint","IMPRINT",FACE,{"disambiguationData":[TD([[makeQuery(id+"F8.imprint","IMPRINT",EDGE,{"derivedFrom":sQuery(id+"F8.wireOp",EDGE,"E218.MirrorCS")}),1.0]])]});
            var Q41;
            Q41=makeQuery(id+"F8.imprint","IMPRINT",FACE,{"disambiguationData":[TD([[makeQuery(id+"F8.imprint","IMPRINT",EDGE,{"derivedFrom":sQuery(id+"F8.wireOp",EDGE,"E233.MirrorCS")}),1.0]])]});
            var Q42;
            Q42=makeQuery(id+"F8.imprint","IMPRINT",FACE,{"disambiguationData":[TD([[makeQuery(id+"F8.imprint","IMPRINT",EDGE,{"derivedFrom":sQuery(id+"F8.wireOp",EDGE,"E211.MirrorCS")}),1.0]])]});
            var Q43;
            Q43=makeQuery(id+"F8.imprint","IMPRINT",FACE,{"disambiguationData":[TD([[makeQuery(id+"F8.imprint","IMPRINT",EDGE,{"derivedFrom":sQuery(id+"F8.wireOp",EDGE,"E181.MirrorCS")}),-1.0]])]});
            var Q44;
            Q44=makeQuery(id+"F8.imprint","IMPRINT",FACE,{"disambiguationData":[TD([[makeQuery(id+"F8.imprint","IMPRINT",EDGE,{"derivedFrom":sQuery(id+"F8.wireOp",EDGE,"E170.MirrorCS")}),-1.0]])]});
            var Q45;
            {var subQ1=sQuery(id+"F8.wireOp",EDGE,"E205.MirrorCS");Q45=makeQuery(id+"F8.imprint","IMPRINT",FACE,{"disambiguationData":[TD([[makeQuery(id+"F8.imprint","IMPRINT",EDGE,{"derivedFrom":subQ1}),-1.0]])]});}
            var Q46;
            {var subQ1=sQuery(id+"F8.wireOp",EDGE,"E263.MirrorCS");Q46=makeQuery(id+"F8.imprint","IMPRINT",FACE,{"disambiguationData":[TD([[makeQuery(id+"F8.imprint","IMPRINT",EDGE,{"derivedFrom":subQ1}),1.0]])]});}
            var Q47;
            Q47=makeQuery(id+"F8.imprint","IMPRINT",FACE,{"disambiguationData":[TD([[makeQuery(id+"F8.imprint","IMPRINT",EDGE,{"derivedFrom":sQuery(id+"F8.wireOp",EDGE,"E295.MirrorCS")}),1.0]])]});
            var Q48;
            {var subQ1=sQuery(id+"F8.wireOp",EDGE,"E263.MirrorCS");Q48=makeQuery(id+"F8.imprint","IMPRINT",FACE,{"disambiguationData":[TD([[makeQuery(id+"F8.imprint","IMPRINT",EDGE,{"derivedFrom":subQ1}),1.0]])]});}
            var Q49;
            Q49=makeQuery(id+"F8.imprint","IMPRINT",FACE,{"disambiguationData":[TD([[makeQuery(id+"F8.imprint","IMPRINT",EDGE,{"derivedFrom":sQuery(id+"F8.wireOp",EDGE,"E284.MirrorCS")}),1.0]])]});
            var Q50;
            Q50=makeQuery(id+"F8.imprint","IMPRINT",FACE,{"disambiguationData":[TD([[makeQuery(id+"F8.imprint","IMPRINT",EDGE,{"derivedFrom":sQuery(id+"F8.wireOp",EDGE,"E149.MirrorCS")}),1.0]])]});
            var Q51;
            Q51=makeQuery(id+"F8.imprint","IMPRINT",FACE,{"disambiguationData":[TD([[makeQuery(id+"F8.imprint","IMPRINT",EDGE,{"derivedFrom":sQuery(id+"F8.wireOp",EDGE,"E134.MirrorCS")}),1.0]])]});
            var Q52;
            Q52=makeQuery(id+"F8.imprint","IMPRINT",FACE,{"disambiguationData":[TD([[makeQuery(id+"F8.imprint","IMPRINT",EDGE,{"derivedFrom":sQuery(id+"F8.wireOp",EDGE,"E145.MirrorCS")}),-1.0]])]});
            var Q53;
            {var subQ1=sQuery(id+"F8.wireOp",EDGE,"E136.MirrorCS");Q53=makeQuery(id+"F8.imprint","IMPRINT",FACE,{"disambiguationData":[TD([[makeQuery(id+"F8.imprint","IMPRINT",EDGE,{"derivedFrom":subQ1}),-1.0]])]});}
            var Q54;
            Q54=makeQuery(id+"F8.imprint","IMPRINT",FACE,{"disambiguationData":[TD([[makeQuery(id+"F8.imprint","IMPRINT",EDGE,{"derivedFrom":sQuery(id+"F8.wireOp",EDGE,"E111.MirrorCS")}),1.0]])]});
            var Q55;
            Q55=makeQuery(id+"F8.imprint","IMPRINT",FACE,{"disambiguationData":[TD([[makeQuery(id+"F8.imprint","IMPRINT",EDGE,{"derivedFrom":sQuery(id+"F8.wireOp",EDGE,"E92.MirrorCS")}),1.0]])]});
            var Q56;
            Q56=makeQuery(id+"F8.imprint","IMPRINT",FACE,{"disambiguationData":[TD([[makeQuery(id+"F8.imprint","IMPRINT",EDGE,{"derivedFrom":sQuery(id+"F8.wireOp",EDGE,"E95.MirrorCS")}),1.0]])]});
            var Q57;
            {var subQ2=sQuery(id+"F8.wireOp",EDGE,"E127.MirrorCS");Q57=makeQuery(id+"F8.imprint","IMPRINT",FACE,{"disambiguationData":[TD([[makeQuery(id+"F8.imprint","IMPRINT",EDGE,{"derivedFrom":subQ2}),-1.0]])]});}
            var Q58;
            Q58=makeQuery(id+"F8.imprint","IMPRINT",FACE,{"disambiguationData":[TD([[makeQuery(id+"F8.imprint","IMPRINT",EDGE,{"derivedFrom":sQuery(id+"F8.wireOp",EDGE,"E116.MirrorCS")}),1.0]])]});
            var Q59;
            Q59=makeQuery(id+"F8.imprint","IMPRINT",FACE,{"disambiguationData":[TD([[makeQuery(id+"F8.imprint","IMPRINT",EDGE,{"derivedFrom":sQuery(id+"F8.wireOp",EDGE,"E129.MirrorCS")}),1.0]])]});
            var Q60;
            Q60=makeQuery(id+"F8.imprint","IMPRINT",FACE,{"disambiguationData":[TD([[makeQuery(id+"F8.imprint","IMPRINT",EDGE,{"derivedFrom":sQuery(id+"F8.wireOp",EDGE,"E88.MirrorCS")}),-1.0]])]});
            var Q61;
            Q61=makeQuery(id+"F8.imprint","IMPRINT",FACE,{"disambiguationData":[TD([[makeQuery(id+"F8.imprint","IMPRINT",EDGE,{"derivedFrom":sQuery(id+"F8.wireOp",EDGE,"E91.MirrorCS")}),-1.0]])]});
            var Q62;
            {var subQ1=sQuery(id+"F8.wireOp",EDGE,"E106.MirrorCS");Q62=makeQuery(id+"F8.imprint","IMPRINT",FACE,{"disambiguationData":[TD([[makeQuery(id+"F8.imprint","IMPRINT",EDGE,{"derivedFrom":subQ1}),-1.0]])]});}
            var Q63;
            {var subQ1=sQuery(id+"F8.wireOp",EDGE,"E143.MirrorCS");Q63=makeQuery(id+"F8.imprint","IMPRINT",FACE,{"disambiguationData":[TD([[makeQuery(id+"F8.imprint","IMPRINT",EDGE,{"derivedFrom":subQ1}),1.0]])]});}
            var Q64;
            Q64=makeQuery(id+"F8.imprint","IMPRINT",FACE,{"disambiguationData":[TD([[makeQuery(id+"F8.imprint","IMPRINT",EDGE,{"derivedFrom":sQuery(id+"F8.wireOp",EDGE,"E141.MirrorCS")}),-1.0]])]});
            var Q65;
            Q65=makeQuery(id+"F8.imprint","IMPRINT",FACE,{"disambiguationData":[TD([[makeQuery(id+"F8.imprint","IMPRINT",EDGE,{"derivedFrom":sQuery(id+"F8.wireOp",EDGE,"E138.MirrorCS")}),1.0]])]});
            var Q66;
            {var subQ1=sQuery(id+"F8.wireOp",EDGE,"E81.MirrorCS");Q66=makeQuery(id+"F8.imprint","IMPRINT",FACE,{"disambiguationData":[TD([[makeQuery(id+"F8.imprint","IMPRINT",EDGE,{"derivedFrom":subQ1}),1.0]])]});}
            var Q67;
            {var subQ1=sQuery(id+"F8.wireOp",EDGE,"E77.MirrorCS");Q67=makeQuery(id+"F8.imprint","IMPRINT",FACE,{"disambiguationData":[TD([[makeQuery(id+"F8.imprint","IMPRINT",EDGE,{"derivedFrom":subQ1}),-1.0]])]});}
            var Q68;
            Q68=makeQuery(id+"F8.imprint","IMPRINT",FACE,{"disambiguationData":[TD([[makeQuery(id+"F8.imprint","IMPRINT",EDGE,{"derivedFrom":sQuery(id+"F8.wireOp",EDGE,"E71.MirrorCS")}),-1.0]])]});
            var Q69;
            {var subQ0=sQuery(id+"F8.wireOp",EDGE,"E73.MirrorCS");Q69=makeQuery(id+"F8.imprint","IMPRINT",FACE,{"disambiguationData":[TD([[makeQuery(id+"F8.imprint","IMPRINT",EDGE,{"derivedFrom":subQ0}),-1.0]])]});}
            var Q70;
            Q70=makeQuery(id+"F8.imprint","IMPRINT",FACE,{"disambiguationData":[TD([[makeQuery(id+"F8.imprint","IMPRINT",EDGE,{"derivedFrom":sQuery(id+"F8.wireOp",EDGE,"E57.MirrorCS")}),-1.0]])]});
            var Q71;
            Q71=makeQuery(id+"F8.imprint","IMPRINT",FACE,{"disambiguationData":[TD([[makeQuery(id+"F8.imprint","IMPRINT",EDGE,{"derivedFrom":sQuery(id+"F8.wireOp",EDGE,"E50.MirrorCS")}),1.0]])]});
            var Q72;
            Q72=makeQuery(id+"F8.imprint","IMPRINT",FACE,{"disambiguationData":[TD([[makeQuery(id+"F8.imprint","IMPRINT",EDGE,{"derivedFrom":sQuery(id+"F8.wireOp",EDGE,"E54.MirrorCS")}),1.0]])]});
            var Q73;
            {var subQ1=sQuery(id+"F8.wireOp",EDGE,"E65.MirrorCS");Q73=makeQuery(id+"F8.imprint","IMPRINT",FACE,{"disambiguationData":[TD([[makeQuery(id+"F8.imprint","IMPRINT",EDGE,{"derivedFrom":subQ1}),-1.0]])]});}
            var Q74;
            Q74=makeQuery(id+"F8.imprint","IMPRINT",FACE,{"disambiguationData":[TD([[makeQuery(id+"F8.imprint","IMPRINT",EDGE,{"derivedFrom":sQuery(id+"F8.wireOp",EDGE,"E32.MirrorCS")}),1.0]])]});
            var Q75;
            Q75=makeQuery(id+"F8.imprint","IMPRINT",FACE,{"disambiguationData":[TD([[makeQuery(id+"F8.imprint","IMPRINT",EDGE,{"derivedFrom":sQuery(id+"F8.wireOp",EDGE,"E31.MirrorCS")}),1.0]])]});
            var Q76;
            Q76=makeQuery(id+"F8.imprint","IMPRINT",FACE,{"disambiguationData":[TD([[makeQuery(id+"F8.imprint","IMPRINT",EDGE,{"derivedFrom":sQuery(id+"F8.wireOp",EDGE,"E29.MirrorCS")}),1.0]])]});
            var Q77;
            Q77=makeQuery(id+"F8.imprint","IMPRINT",FACE,{"disambiguationData":[TD([[makeQuery(id+"F8.imprint","IMPRINT",EDGE,{"derivedFrom":sQuery(id+"F8.wireOp",EDGE,"E36.MirrorCS")}),1.0]])]});
            var Q78;
            Q78=makeQuery(id+"F8.imprint","IMPRINT",FACE,{"disambiguationData":[TD([[makeQuery(id+"F8.imprint","IMPRINT",EDGE,{"derivedFrom":sQuery(id+"F8.wireOp",EDGE,"E37.MirrorCS")}),-1.0]])]});
            var Q79;
            {var subQ1=sQuery(id+"F8.wireOp",EDGE,"E21.MirrorCS");Q79=makeQuery(id+"F8.imprint","IMPRINT",FACE,{"disambiguationData":[TD([[makeQuery(id+"F8.imprint","IMPRINT",EDGE,{"derivedFrom":subQ1}),-1.0]])]});}
            var Q80;
            {var subQ1=sQuery(id+"F8.wireOp",EDGE,"E16.MirrorCS");Q80=makeQuery(id+"F8.imprint","IMPRINT",FACE,{"disambiguationData":[TD([[makeQuery(id+"F8.imprint","IMPRINT",EDGE,{"derivedFrom":subQ1}),1.0]])]});}
            var Q81;
            {var subQ1=sQuery(id+"F8.wireOp",EDGE,"E11");Q81=makeQuery(id+"F8.imprint","IMPRINT",FACE,{"disambiguationData":[TD([[makeQuery(id+"F8.imprint","IMPRINT",EDGE,{"derivedFrom":subQ1}),-1.0]])]});}
            var Q82;
            {var subQ0=sQuery(id+"F8.wireOp",EDGE,"E8");Q82=makeQuery(id+"F8.imprint","IMPRINT",FACE,{"disambiguationData":[TD([[makeQuery(id+"F8.imprint","IMPRINT",EDGE,{"derivedFrom":subQ0}),-1.0]])]});}
            extrude(context, id + "F9", {"entities" : qUnion([Q0, Q1, Q2, Q3, Q4, Q5, Q6, Q7, Q8, Q9, Q10, Q11, Q12, Q13, Q14, Q15, Q16, Q17, Q18, Q19, Q20, Q21, Q22, Q23, Q24, Q25, Q26, Q27, Q28, Q29, Q30, Q31, Q32, Q33, Q34, Q35, Q36, Q37, Q38, Q39, Q40, Q41, Q42, Q43, Q44, Q45, Q46, Q47, Q48, Q49, Q50, Q51, Q52, Q53, Q54, Q55, Q56, Q57, Q58, Q59, Q60, Q61, Q62, Q63, Q64, Q65, Q66, Q67, Q68, Q69, Q70, Q71, Q72, Q73, Q74, Q75, Q76, Q77, Q78, Q79, Q80, Q81, Q82]), "operationType" : NewBodyOperationType.REMOVE, "oppositeDirection" : true, "depth" : 25.4 * mm});
        }
        {
            var Q0;
            Q0=makeQuery(id+"F9.boolean.opBoolean","COPY",EDGE,{"derivedFrom":makeQuery(id+"F9.opExtrude","SWEPT_EDGE",EDGE,{"disambiguationData":[OSD([sQuery(id+"F6.wireOp",EDGE,"E4"),sQuery(id+"F6.wireOp",EDGE,"E5"),sQuery(id+"F8.wireOp",EDGE,"E397.MirrorCS"),sQuery(id+"F8.wireOp",EDGE,"E409.MirrorCS")])]})});
            var Q1;
            Q1=makeQuery(id+"F9.boolean.opBoolean","COPY",EDGE,{"derivedFrom":makeQuery(id+"F9.opExtrude","SWEPT_EDGE",EDGE,{"disambiguationData":[OSD([sQuery(id+"F6.wireOp",EDGE,"E4"),sQuery(id+"F6.wireOp",EDGE,"E5"),sQuery(id+"F8.wireOp",EDGE,"E397.MirrorCS"),sQuery(id+"F8.wireOp",EDGE,"E401.MirrorCS")])]})});
            var Q2;
            Q2=makeQuery(id+"F9.boolean.opBoolean","COPY",EDGE,{"derivedFrom":makeQuery(id+"F9.opExtrude","SWEPT_EDGE",EDGE,{"disambiguationData":[OSD([sQuery(id+"F8.wireOp",EDGE,"E393.MirrorCS"),sQuery(id+"F8.wireOp",EDGE,"E401.MirrorCS")])]})});
            var Q3;
            Q3=makeQuery(id+"F9.boolean.opBoolean","COPY",EDGE,{"derivedFrom":makeQuery(id+"F9.opExtrude","SWEPT_EDGE",EDGE,{"disambiguationData":[OSD([sQuery(id+"F8.wireOp",EDGE,"E408.MirrorCS"),sQuery(id+"F8.wireOp",EDGE,"E409.MirrorCS")])]})});
            var Q4;
            Q4=makeQuery(id+"F9.boolean.opBoolean","COPY",EDGE,{"derivedFrom":makeQuery(id+"F9.opExtrude","SWEPT_EDGE",EDGE,{"disambiguationData":[OSD([sQuery(id+"F8.wireOp",EDGE,"E394.MirrorCS"),sQuery(id+"F8.wireOp",EDGE,"E405.MirrorCS")])]})});
            var Q5;
            Q5=makeQuery(id+"F9.boolean.opBoolean","COPY",EDGE,{"derivedFrom":makeQuery(id+"F9.opExtrude","SWEPT_EDGE",EDGE,{"disambiguationData":[OSD([sQuery(id+"F6.wireOp",EDGE,"E4"),sQuery(id+"F6.wireOp",EDGE,"E5"),sQuery(id+"F8.wireOp",EDGE,"E398.MirrorCS"),sQuery(id+"F8.wireOp",EDGE,"E405.MirrorCS")])]})});
            var Q6;
            Q6=makeQuery(id+"F9.boolean.opBoolean","COPY",EDGE,{"derivedFrom":makeQuery(id+"F9.opExtrude","SWEPT_EDGE",EDGE,{"disambiguationData":[OSD([sQuery(id+"F6.wireOp",EDGE,"E4"),sQuery(id+"F6.wireOp",EDGE,"E5"),sQuery(id+"F8.wireOp",EDGE,"E398.MirrorCS"),sQuery(id+"F8.wireOp",EDGE,"E404.MirrorCS")])]})});
            var Q7;
            Q7=makeQuery(id+"F9.boolean.opBoolean","COPY",EDGE,{"derivedFrom":makeQuery(id+"F9.opExtrude","SWEPT_EDGE",EDGE,{"disambiguationData":[OSD([sQuery(id+"F8.wireOp",EDGE,"E400.MirrorCS"),sQuery(id+"F8.wireOp",EDGE,"E404.MirrorCS")])]})});
            var Q8;
            Q8=makeQuery(id+"F9.boolean.opBoolean","COPY",EDGE,{"derivedFrom":makeQuery(id+"F9.opExtrude","SWEPT_EDGE",EDGE,{"disambiguationData":[OSD([sQuery(id+"F8.wireOp",EDGE,"E396.MirrorCS"),sQuery(id+"F8.wireOp",EDGE,"E406.MirrorCS")])]})});
            var Q9;
            Q9=makeQuery(id+"F9.boolean.opBoolean","COPY",EDGE,{"derivedFrom":makeQuery(id+"F9.opExtrude","SWEPT_EDGE",EDGE,{"disambiguationData":[OSD([sQuery(id+"F6.wireOp",EDGE,"E4"),sQuery(id+"F6.wireOp",EDGE,"E5"),sQuery(id+"F8.wireOp",EDGE,"E399.MirrorCS"),sQuery(id+"F8.wireOp",EDGE,"E406.MirrorCS")])]})});
            var Q10;
            Q10=makeQuery(id+"F9.boolean.opBoolean","COPY",EDGE,{"derivedFrom":makeQuery(id+"F9.opExtrude","SWEPT_EDGE",EDGE,{"disambiguationData":[OSD([sQuery(id+"F6.wireOp",EDGE,"E4"),sQuery(id+"F6.wireOp",EDGE,"E5"),sQuery(id+"F8.wireOp",EDGE,"E399.MirrorCS"),sQuery(id+"F8.wireOp",EDGE,"E403.MirrorCS")])]})});
            var Q11;
            Q11=makeQuery(id+"F9.boolean.opBoolean","COPY",EDGE,{"derivedFrom":makeQuery(id+"F9.opExtrude","SWEPT_EDGE",EDGE,{"disambiguationData":[OSD([sQuery(id+"F8.wireOp",EDGE,"E392.MirrorCS"),sQuery(id+"F8.wireOp",EDGE,"E403.MirrorCS")])]})});
            fillet(context, id + "F10", {"entities" : qUnion([Q0, Q1, Q2, Q3, Q4, Q5, Q6, Q7, Q8, Q9, Q10, Q11]), "radius" : 0.38 * mm, "tangentPropagation" : true, "allowEdgeOverflow" : false});
        }
    });
